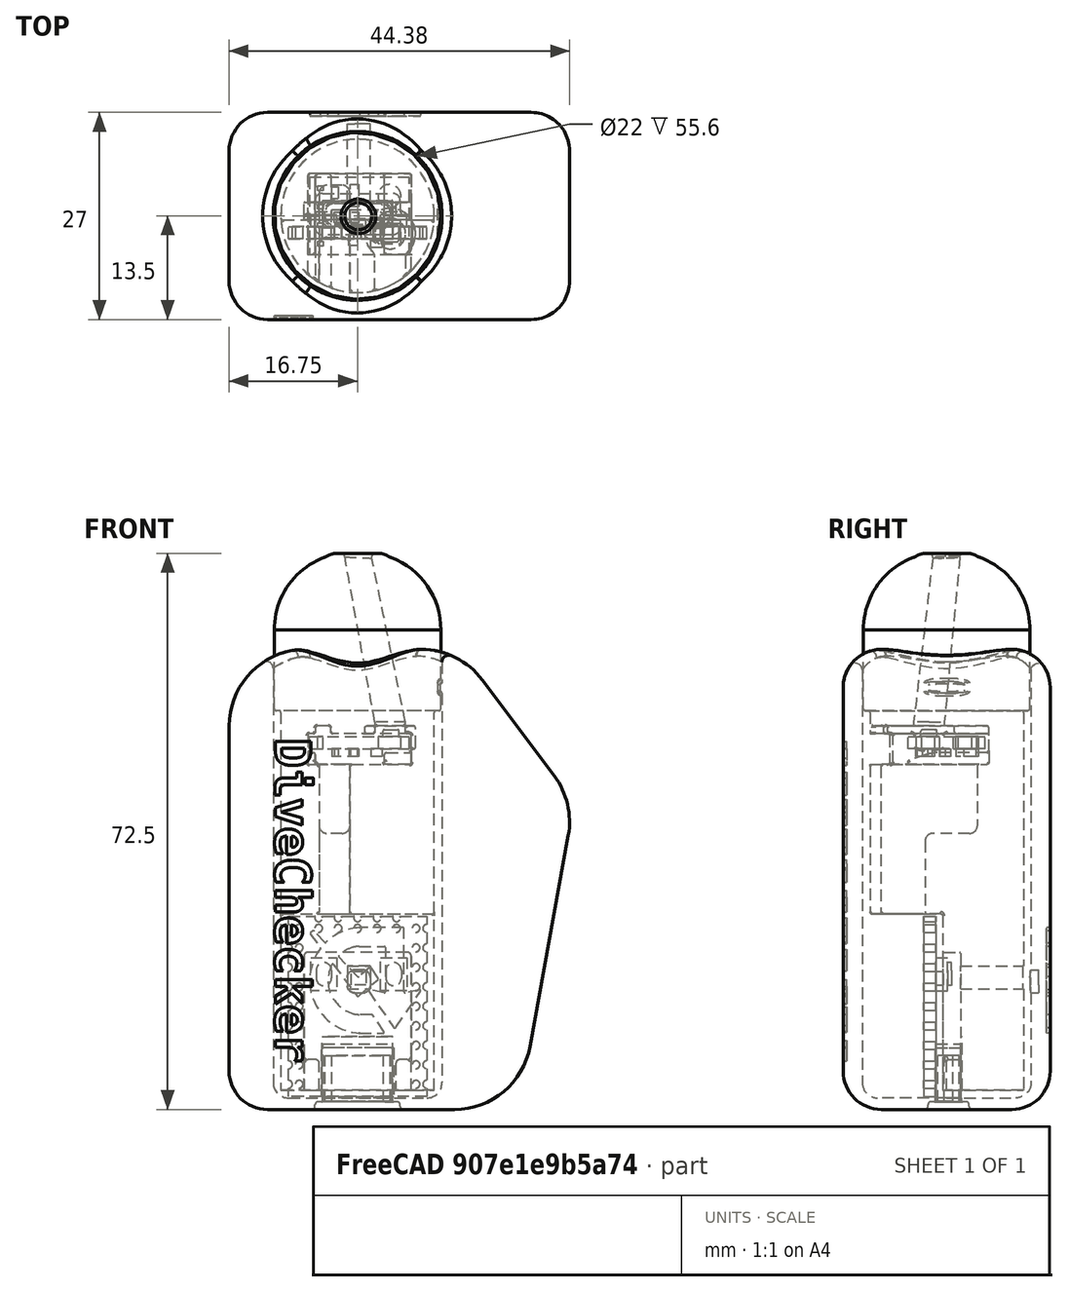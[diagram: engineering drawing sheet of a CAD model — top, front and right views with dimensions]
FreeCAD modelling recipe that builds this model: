
FCSTD DOCUMENT  (FreeCAD 1.0R39319 (Git))
Label: Device_V11
License: All rights reserved
objects: PartDesign::Fillet×55, Sketcher::SketchObject×35, PartDesign::Pocket×26, PartDesign::Pad×14, PartDesign::Revolution×2, Part::Feature×2, PartDesign::SubtractiveLoft×2, PartDesign::Body×2, PartDesign::SubtractivePipe×1, PartDesign::Chamfer×1, Image::ImagePlane×1, Part::Part2DObjectPython×1
note: 378 computed .brp shape members not serialized (recipe doc carries the construction recipe); baked Part::Feature solids carry a one-line shape summary decoded from their .brp

FEATURE [Sketcher::SketchObject] Sketch
  ArcFitTolerance = 1e-06
  AttachmentSupport = -> [XZ_Plane]
  FullyConstrained = true
  MakeInternals = false
  MapMode = 5
  Placement = pos=(0,0,0) rot=(1,0,0;1.5708rad)
  sketch-geometry (8):
    g0: LineSegment [constr] StartX=0 StartY=0 StartZ=0 EndX=0 EndY=75 EndZ=0
    g1: LineSegment StartX=0 StartY=75 StartZ=0 EndX=30 EndY=75 EndZ=0
    g2: LineSegment StartX=30 StartY=75 StartZ=0 EndX=45 EndY=55 EndZ=0
    g3: LineSegment [constr] StartX=45 StartY=55 StartZ=0 EndX=35 EndY=0 EndZ=0
    g4: LineSegment [constr] StartX=35 StartY=0 StartZ=0 EndX=0 EndY=0 EndZ=0
    g5: LineSegment StartX=0 StartY=75 StartZ=0 EndX=0 EndY=15 EndZ=0
    g6: LineSegment StartX=0 StartY=15 StartZ=0 EndX=37.7273 EndY=15 EndZ=0
    g7: LineSegment StartX=37.7273 StartY=15 StartZ=0 EndX=45 EndY=55 EndZ=0
  constraints (22):
    c: Coincident(g-1,g0)
    c: Coincident(g0,g1)
    c: Horizontal(g1)
    c: Coincident(g1,g2)
    c: Coincident(g2,g3)
    c: Coincident(g3,g4)
    c: Coincident(g4,g0)
    c: Vertical(g0)
    c: Horizontal(g4)
    c: DistanceX(g4,g4) = 35
    c: DistanceX(g1,g1) = 30
    c: DistanceY(g0,g0) = 75
    c: DistanceY(g2,g1) = 20
    c: DistanceX(g0,g2) = 45
    c: Coincident(g5,g0)
    c: Coincident(g6,g5)
    c: Horizontal(g6)
    c: Coincident(g7,g6)
    c: Coincident(g7,g2)
    c: PointOnObject(g6,g3)
    c: Vertical(g5)
    c: DistanceY(g0,g5) = 15
FEATURE [PartDesign::Pad] Pad
  Direction = (0,-1,2e-16)
  Length = 27
  Length2 = 10
  Midplane = true
  Placement = pos=(0,0,0) rot=(1,0,0;1.5708rad)
  Profile = -> Sketch
  ReferenceAxis = -> Sketch [N_Axis]
  Refine = true
  Suppressed = false
  Type = 0
FEATURE [PartDesign::Fillet] Fillet
  Base = -> Pad [Edge2,Edge5,Edge8,Edge1]
  BaseFeature = -> Pad
  Placement = pos=(0,0,0) rot=(1,0,0;1.5708rad)
  Radius = 10
  Refine = true
  SupportTransform = false
  Suppressed = false
  UseAllEdges = false
FEATURE [PartDesign::Fillet] Fillet001
  Base = -> Fillet [Edge18,Edge8,Edge23]
  BaseFeature = -> Fillet
  Placement = pos=(0,0,0) rot=(1,0,0;1.5708rad)
  Radius = 5
  Refine = true
  SupportTransform = false
  Suppressed = false
  UseAllEdges = false
FEATURE [Sketcher::SketchObject] Sketch003
  ArcFitTolerance = 1e-06
  AttachmentSupport = -> [XZ_Plane001]
  FullyConstrained = true
  MakeInternals = false
  MapMode = 5
  Placement = pos=(0,0,0) rot=(1,0,0;1.5708rad)
  sketch-geometry (9):
    g0: LineSegment StartX=19 StartY=87 StartZ=0 EndX=19 EndY=77 EndZ=0
    g1: LineSegment StartX=19 StartY=77 StartZ=0 EndX=27.5 EndY=77 EndZ=0
    g2: LineSegment StartX=19 StartY=87 StartZ=0 EndX=20 EndY=87 EndZ=0
    g3: LineSegment StartX=20 StartY=87 StartZ=0 EndX=21 EndY=86.5 EndZ=0
    g4: ArcOfCircle CenterX=17.4538 CenterY=77.1 CenterZ=0 NormalX=0 NormalY=0 NormalZ=1 AngleXU=0 Radius=10.0467 StartAngle=6.27323 EndAngle=7.49324
    g5: LineSegment [constr] StartX=0 StartY=0 StartZ=0 EndX=27.5 EndY=0 EndZ=0
    g6: LineSegment [constr] StartX=27.5 StartY=0 StartZ=0 EndX=27.5 EndY=77 EndZ=0
    g7: LineSegment [constr] StartX=27.5 StartY=77 StartZ=0 EndX=0 EndY=77 EndZ=0
    g8: LineSegment [constr] StartX=0 StartY=77 StartZ=0 EndX=0 EndY=0 EndZ=0
  constraints (26):
    c: Vertical(g0)
    c: Coincident(g0,g1)
    c: Horizontal(g1)
    c: Coincident(g0,g2)
    c: Horizontal(g2)
    c: Coincident(g2,g3)
    c: Coincident(g4,g3)
    c: Coincident(g4,g1)
    c: DistanceY(g0,g0) = 10
    c: DistanceY(g3,g2) = 0.5
    c: DistanceX(g2,g2) = 1
    c: DistanceX(g2,g3) = 1
    c: DistanceX(g1,g1) = 8.5
    c: Coincident(g5,g6)
    c: Coincident(g6,g7)
    c: Coincident(g7,g8)
    c: Coincident(g8,g5)
    c: Horizontal(g5)
    c: Horizontal(g7)
    c: Vertical(g6)
    c: Vertical(g8)
    c: Coincident(g5,g-1)
    c: Coincident(g6,g1)
    c: DistanceY(g8,g8) = 77
    c: DistanceX(g7,g7) = 27.5
    c: DistanceY(g0,g4) = 0.1
FEATURE [Sketcher::SketchObject] Sketch004
  ArcFitTolerance = 1e-06
  AttachmentSupport = -> [XZ_Plane001]
  FullyConstrained = true
  MakeInternals = false
  MapMode = 5
  Placement = pos=(0,0,0) rot=(1,0,0;1.5708rad)
  sketch-geometry (7):
    g0: LineSegment StartX=16.75 StartY=87 StartZ=0 EndX=16.75 EndY=77 EndZ=0
    g1: LineSegment [constr] StartX=0 StartY=0 StartZ=0 EndX=27.5 EndY=0 EndZ=0
    g2: LineSegment [constr] StartX=27.5 StartY=0 StartZ=0 EndX=27.5 EndY=77 EndZ=0
    g3: LineSegment [constr] StartX=27.5 StartY=77 StartZ=0 EndX=0 EndY=77 EndZ=0
    g4: LineSegment [constr] StartX=0 StartY=77 StartZ=0 EndX=0 EndY=0 EndZ=0
    g5: GeomPoint [constr] X=10 Y=77 Z=0
    g6: GeomPoint [constr] X=23.5 Y=77 Z=0
  constraints (18):
    c: Vertical(g0)
    c: DistanceY(g0,g0) = 10
    c: Coincident(g1,g2)
    c: Coincident(g2,g3)
    c: Coincident(g3,g4)
    c: Coincident(g4,g1)
    c: Horizontal(g1)
    c: Horizontal(g3)
    c: Vertical(g2)
    c: Vertical(g4)
    c: Coincident(g1,g-1)
    c: DistanceY(g4,g4) = 77
    c: DistanceX(g3,g3) = 27.5
    c: PointOnObject(g5,g3)
    c: PointOnObject(g6,g3)
    c: DistanceX(g6,g2) = 4
    c: DistanceX(g3,g5) = 10
    c: Symmetric(g5,g6,g0)
FEATURE [PartDesign::Revolution] Revolution
  Angle = 360
  Angle2 = 60
  Axis = (0,-2e-16,-1)
  Base = (16.75,1.93e-14,87)
  Placement = pos=(0,0,0) rot=(1,0,0;1.5708rad)
  Profile = -> Sketch003
  ReferenceAxis = -> Sketch004 [Edge1]
  Refine = true
  Reversed = true
  Suppressed = false
  Type = 0
FEATURE [PartDesign::Pad] Pad001
  BaseFeature = -> Revolution
  Direction = (0,-2e-16,-1)
  Length = 61
  Length2 = 10
  Placement = pos=(0,0,0) rot=(1,0,0;1.5708rad)
  Profile = -> Revolution [Face2]
  Refine = true
  Suppressed = false
  Type = 0
FEATURE [Sketcher::SketchObject] Sketch006
  ArcFitTolerance = 1e-06
  AttachmentOffset = pos=(0,0,-25) rot=(0,0,1;0rad)
  AttachmentSupport = -> [Fillet001]
  FullyConstrained = true
  MakeInternals = false
  MapMode = 5
  Placement = pos=(0,6.6e-15,40) rot=(1,0,0;3.14159rad)
  sketch-geometry (1):
    g0: Circle CenterX=16.75 CenterY=0 CenterZ=0 NormalX=0 NormalY=0 NormalZ=1 AngleXU=0 Radius=11
  constraints (3):
    c: PointOnObject(g0,g-1)
    c: DistanceX(g-1,g0) = 16.75
    c: Diameter(g0) = 22
FEATURE [PartDesign::Pocket] Pocket
  BaseFeature = -> Fillet001
  Direction = (0,0,1)
  Length = 5
  Length2 = 5
  Placement = pos=(0,0,0) rot=(1,0,0;1.5708rad)
  Profile = -> Sketch006
  ReferenceAxis = -> Sketch006 [N_Axis]
  Refine = true
  Suppressed = false
  Type = 1
FEATURE [Part::Feature] Part__Feature  label="RP2350-Zero-mini"
  Placement = pos=(7.75,-3,40.2) rot=(1,0,0;4.71239rad)
  shape: bbox 18 x 4.88 x 24.16 mm, 130 faces (baked)
FEATURE [Sketcher::SketchObject] Sketch008
  ArcFitTolerance = 1e-06
  AttachmentSupport = -> [Pocket]
  ExternalGeometry = -> [Pocket]
  FullyConstrained = true
  MakeInternals = false
  MapMode = 5
  Placement = pos=(0,0,40) rot=(0,0,1;3.14159rad)
  sketch-geometry (19):
    g0: LineSegment [constr] StartX=-25.85 StartY=5.5 StartZ=0 EndX=-7.65 EndY=5.5 EndZ=0
    g1: LineSegment StartX=-7.65 StartY=5.5 StartZ=0 EndX=-7.65 EndY=1.3 EndZ=0
    g2: LineSegment [constr] StartX=-7.65 StartY=1.3 StartZ=0 EndX=-9.75 EndY=1.3 EndZ=0
    g3: LineSegment [constr] StartX=-9.75 StartY=1.3 StartZ=0 EndX=-9.75 EndY=-1.5 EndZ=0
    g4: LineSegment [constr] StartX=-9.75 StartY=-1.5 StartZ=0 EndX=-11.75 EndY=-1.5 EndZ=0
    g5: LineSegment [constr] StartX=-11.75 StartY=-1.5 StartZ=0 EndX=-11.75 EndY=-2.5 EndZ=0
    g6: LineSegment StartX=-11.75 StartY=-2.5 StartZ=0 EndX=-21.75 EndY=-2.5 EndZ=0
    g7: LineSegment [constr] StartX=-21.75 StartY=-2.5 StartZ=0 EndX=-21.75 EndY=-1.5 EndZ=0
    g8: LineSegment [constr] StartX=-21.75 StartY=-1.5 StartZ=0 EndX=-23.75 EndY=-1.5 EndZ=0
    g9: LineSegment [constr] StartX=-23.75 StartY=-1.5 StartZ=0 EndX=-23.75 EndY=1.3 EndZ=0
    g10: LineSegment [constr] StartX=-23.75 StartY=1.3 StartZ=0 EndX=-25.85 EndY=1.3 EndZ=0
    g11: LineSegment StartX=-25.85 StartY=1.3 StartZ=0 EndX=-25.85 EndY=5.5 EndZ=0
    g12: LineSegment StartX=-25.85 StartY=5.5 StartZ=0 EndX=-20.85 EndY=3.5 EndZ=0
    g13: LineSegment StartX=-20.85 StartY=3.5 StartZ=0 EndX=-12.65 EndY=3.5 EndZ=0
    g14: LineSegment StartX=-12.65 StartY=3.5 StartZ=0 EndX=-7.65 EndY=5.5 EndZ=0
    g15: LineSegment StartX=-25.85 StartY=1.3 StartZ=0 EndX=-21.75 EndY=1.3 EndZ=0
    g16: LineSegment StartX=-21.75 StartY=1.3 StartZ=0 EndX=-21.75 EndY=-2.5 EndZ=0
    g17: LineSegment StartX=-11.75 StartY=-2.5 StartZ=0 EndX=-11.75 EndY=1.3 EndZ=0
    g18: LineSegment StartX=-11.75 StartY=1.3 StartZ=0 EndX=-7.65 EndY=1.3 EndZ=0
  constraints (54):
    c: Horizontal(g0)
    c: Coincident(g0,g1)
    c: Vertical(g1)
    c: Coincident(g1,g2)
    c: Horizontal(g2)
    c: Coincident(g2,g3)
    c: Vertical(g3)
    c: Coincident(g3,g4)
    c: Horizontal(g4)
    c: Coincident(g4,g5)
    c: Vertical(g5)
    c: Coincident(g5,g6)
    c: Horizontal(g6)
    c: Coincident(g6,g7)
    c: Vertical(g7)
    c: Coincident(g7,g8)
    c: Horizontal(g8)
    c: Coincident(g8,g9)
    c: Vertical(g9)
    c: Coincident(g9,g10)
    c: Horizontal(g10)
    c: Coincident(g10,g11)
    c: Vertical(g11)
    c: Coincident(g0,g11)
    c: DistanceX(g0,g-3) = 9.1
    c: DistanceX(g0,g0) = 18.2
    c: DistanceY(g-3,g1) = 1.3
    c: Horizontal(g2,g9)
    c: DistanceX(g8,g-3) = 7
    c: DistanceX(g-3,g3) = 7
    c: DistanceY(g3,g-3) = 1.5
    c: Horizontal(g3,g7)
    c: DistanceX(g7,g-3) = 5
    c: DistanceX(g-3,g4) = 5
    c: DistanceY(g5,g-3) = 2.5
    c: DistanceY(g-3,g0) = 5.5
    c: Coincident(g0,g12)
    c: Coincident(g12,g13)
    c: Horizontal(g13)
    c: Coincident(g13,g14)
    c: Coincident(g14,g0)
    c: DistanceX(g13,g0) = 5
    c: DistanceX(g0,g12) = 5
    c: DistanceY(g12,g0) = 2
    c: Coincident(g15,g10)
    c: Horizontal(g15)
    c: Coincident(g16,g15)
    c: Coincident(g16,g6)
    c: Vertical(g16)
    c: Coincident(g17,g5)
    c: Vertical(g17)
    c: Coincident(g18,g17)
    c: Coincident(g18,g1)
    c: Horizontal(g18)
FEATURE [PartDesign::Pocket] Pocket001
  BaseFeature = -> Pocket
  Direction = (0,0,-1)
  Length = 24
  Length2 = 5
  Placement = pos=(0,0,0) rot=(1,0,0;1.5708rad)
  Profile = -> Sketch008
  ReferenceAxis = -> Sketch008 [N_Axis]
  Refine = true
  Suppressed = false
  Type = 0
FEATURE [Sketcher::SketchObject] Sketch009
  ArcFitTolerance = 1e-06
  AttachmentSupport = -> [Pocket001]
  ExternalGeometry = -> [Pocket001]
  FullyConstrained = true
  MakeInternals = false
  MapMode = 5
  Placement = pos=(0,0,40) rot=(0,0,1;3.14159rad)
  sketch-geometry (8):
    g0: LineSegment StartX=-21.75 StartY=1.3 StartZ=0 EndX=-23.45 EndY=1.3 EndZ=0
    g1: LineSegment StartX=-23.45 StartY=1.3 StartZ=0 EndX=-23.45 EndY=-1.7 EndZ=0
    g2: LineSegment StartX=-23.45 StartY=-1.7 StartZ=0 EndX=-21.75 EndY=-1.7 EndZ=0
    g3: LineSegment StartX=-21.75 StartY=-1.7 StartZ=0 EndX=-21.75 EndY=1.3 EndZ=0
    g4: LineSegment StartX=-11.75 StartY=1.3 StartZ=0 EndX=-11.75 EndY=-1.7 EndZ=0
    g5: LineSegment StartX=-11.75 StartY=-1.7 StartZ=0 EndX=-10.05 EndY=-1.7 EndZ=0
    g6: LineSegment StartX=-10.05 StartY=-1.7 StartZ=0 EndX=-10.05 EndY=1.3 EndZ=0
    g7: LineSegment StartX=-10.05 StartY=1.3 StartZ=0 EndX=-11.75 EndY=1.3 EndZ=0
  constraints (22):
    c: Coincident(g0,g1)
    c: Coincident(g1,g2)
    c: Coincident(g2,g3)
    c: Coincident(g3,g0)
    c: Horizontal(g0)
    c: Horizontal(g2)
    c: Vertical(g1)
    c: Vertical(g3)
    c: Coincident(g0,g-3)
    c: DistanceY(g1,g1) = 3
    c: DistanceX(g2,g2) = 1.7
    c: Coincident(g4,g5)
    c: Coincident(g5,g6)
    c: Coincident(g6,g7)
    c: Coincident(g7,g4)
    c: Vertical(g4)
    c: Vertical(g6)
    c: Horizontal(g5)
    c: Horizontal(g7)
    c: Coincident(g4,g-4)
    c: Equal(g2,g5)
    c: Equal(g1,g6)
FEATURE [PartDesign::Pocket] Pocket002
  BaseFeature = -> Pocket001
  Direction = (0,0,-1)
  Length = 16
  Length2 = 5
  Placement = pos=(0,0,0) rot=(1,0,0;1.5708rad)
  Profile = -> Sketch009
  ReferenceAxis = -> Sketch009 [N_Axis]
  Refine = true
  Suppressed = false
  Type = 0
FEATURE [Sketcher::SketchObject] Sketch010
  ArcFitTolerance = 1e-06
  AttachmentSupport = -> [Pocket002]
  ExternalGeometry = -> [Pocket002]
  FullyConstrained = true
  MakeInternals = false
  MapMode = 5
  Placement = pos=(0,6.6e-15,15) rot=(1,0,0;3.14159rad)
  sketch-geometry (4):
    g0: LineSegment StartX=12.2 StartY=1.45 StartZ=0 EndX=12.2 EndY=-1.94 EndZ=0
    g1: LineSegment StartX=12.2 StartY=-1.94 StartZ=0 EndX=21.3 EndY=-1.94 EndZ=0
    g2: LineSegment StartX=21.3 StartY=-1.94 StartZ=0 EndX=21.3 EndY=1.45 EndZ=0
    g3: LineSegment StartX=21.3 StartY=1.45 StartZ=0 EndX=12.2 EndY=1.45 EndZ=0
  constraints (12):
    c: Coincident(g0,g1)
    c: Coincident(g1,g2)
    c: Coincident(g2,g3)
    c: Coincident(g3,g0)
    c: Vertical(g0)
    c: Vertical(g2)
    c: Horizontal(g1)
    c: Horizontal(g3)
    c: DistanceY(g2,g2) = 3.39
    c: DistanceX(g3,g3) = 9.1
    c: DistanceX(g-5,g0) = 0.45
    c: DistanceY(g-4,g1) = 0.56
FEATURE [PartDesign::Pocket] Pocket003
  BaseFeature = -> Pocket002
  Direction = (0,0,1)
  Length = 1
  Length2 = 5
  Placement = pos=(0,0,0) rot=(1,0,0;1.5708rad)
  Profile = -> Sketch010
  ReferenceAxis = -> Sketch010 [N_Axis]
  Refine = true
  Suppressed = false
  Type = 0
FEATURE [PartDesign::Fillet] Fillet002
  Base = -> Pocket003 [Edge141,Edge140]
  BaseFeature = -> Pocket003
  Placement = pos=(0,0,0) rot=(1,0,0;1.5708rad)
  Radius = 1
  Refine = true
  SupportTransform = false
  Suppressed = false
  UseAllEdges = false
FEATURE [PartDesign::Fillet] Fillet003
  Base = -> Fillet002 [Edge16,Edge12]
  BaseFeature = -> Fillet002
  Placement = pos=(0,0,0) rot=(1,0,0;1.5708rad)
  Radius = 1
  Refine = true
  SupportTransform = false
  Suppressed = false
  UseAllEdges = false
FEATURE [PartDesign::Fillet] Fillet004
  Base = -> Fillet003 [Edge85,Edge101]
  BaseFeature = -> Fillet003
  Placement = pos=(0,0,0) rot=(1,0,0;1.5708rad)
  Radius = 1
  Refine = true
  SupportTransform = false
  Suppressed = false
  UseAllEdges = false
FEATURE [PartDesign::Fillet] Fillet005
  Base = -> Fillet004 [Edge33,Edge36]
  BaseFeature = -> Fillet004
  Placement = pos=(0,0,0) rot=(1,0,0;1.5708rad)
  Radius = 0.5
  Refine = true
  SupportTransform = false
  Suppressed = false
  UseAllEdges = false
FEATURE [PartDesign::Fillet] Fillet006
  Base = -> Fillet005 [Edge85,Edge82]
  BaseFeature = -> Fillet005
  Placement = pos=(0,0,0) rot=(1,0,0;1.5708rad)
  Radius = 0.5
  Refine = true
  SupportTransform = false
  Suppressed = false
  UseAllEdges = false
FEATURE [PartDesign::Fillet] Fillet007
  Base = -> Fillet006 [Edge24,Edge56]
  BaseFeature = -> Fillet006
  Placement = pos=(0,0,0) rot=(1,0,0;1.5708rad)
  Radius = 0.25
  Refine = true
  SupportTransform = false
  Suppressed = false
  UseAllEdges = false
FEATURE [PartDesign::Fillet] Fillet008
  Base = -> Fillet007 [Edge38,Edge95]
  BaseFeature = -> Fillet007
  Placement = pos=(0,0,0) rot=(1,0,0;1.5708rad)
  Radius = 0.5
  Refine = true
  SupportTransform = false
  Suppressed = false
  UseAllEdges = false
FEATURE [PartDesign::Fillet] Fillet009
  Base = -> Fillet008 [Edge79,Edge60]
  BaseFeature = -> Fillet008
  Placement = pos=(0,0,0) rot=(1,0,0;1.5708rad)
  Radius = 0.13
  Refine = true
  SupportTransform = false
  Suppressed = false
  UseAllEdges = false
FEATURE [Part::Feature] Part__Feature001  label="BME280-5V"
  Placement = pos=(10.5,-5,62) rot=(0,0,1;0rad)
  shape: bbox 13 x 10 x 3.53 mm, 88 faces (baked)
FEATURE [Sketcher::SketchObject] Sketch012
  ArcFitTolerance = 1e-06
  AttachmentSupport = -> [XZ_Plane001]
  FullyConstrained = true
  MakeInternals = false
  MapMode = 5
  Placement = pos=(0,0,0) rot=(1,0,0;1.5708rad)
  sketch-geometry (4):
    g0: LineSegment StartX=10.25 StartY=63.5 StartZ=0 EndX=10.25 EndY=59.5 EndZ=0
    g1: LineSegment StartX=10.25 StartY=59.5 StartZ=0 EndX=23.75 EndY=59.5 EndZ=0
    g2: LineSegment StartX=23.75 StartY=59.5 StartZ=0 EndX=23.75 EndY=63.5 EndZ=0
    g3: LineSegment StartX=23.75 StartY=63.5 StartZ=0 EndX=10.25 EndY=63.5 EndZ=0
  constraints (12):
    c: Coincident(g0,g1)
    c: Coincident(g1,g2)
    c: Coincident(g2,g3)
    c: Coincident(g3,g0)
    c: Vertical(g0)
    c: Vertical(g2)
    c: Horizontal(g1)
    c: Horizontal(g3)
    c: Distance(g0,g2) = 13.5
    c: Distance(g1,g3) = 4
    c: DistanceY(g-1,g0) = 59.5
    c: DistanceX(g-1,g0) = 10.25
FEATURE [PartDesign::Pocket] Pocket004
  BaseFeature = -> Pad001
  Direction = (0,1,-2e-16)
  Length = 5
  Length2 = 13
  Placement = pos=(0,0,0) rot=(1,0,0;1.5708rad)
  Profile = -> Sketch012
  ReferenceAxis = -> Sketch012 [N_Axis]
  Refine = true
  Suppressed = false
  Type = 4
FEATURE [Sketcher::SketchObject] Sketch013
  ArcFitTolerance = 1e-06
  AttachmentSupport = -> [Pocket004]
  FullyConstrained = true
  MakeInternals = false
  MapMode = 5
  Placement = pos=(0,2.79e-14,63.5) rot=(1,0,0;3.14159rad)
  sketch-geometry (2):
    g0: Circle CenterX=21 CenterY=2.3 CenterZ=0 NormalX=0 NormalY=0 NormalZ=1 AngleXU=0 Radius=2
    g1: Circle CenterX=21 CenterY=2.3 CenterZ=0 NormalX=0 NormalY=0 NormalZ=1 AngleXU=0 Radius=3.3
  constraints (5):
    c: Diameter(g0) = 4
    c: DistanceY(g-1,g0) = 2.3
    c: DistanceX(g-1,g0) = 21
    c: Diameter(g1) = 6.6
    c: Coincident(g1,g0)
FEATURE [Sketcher::SketchObject] Sketch015
  ArcFitTolerance = 1e-06
  AttachmentSupport = -> [Pocket004]
  ExternalGeometry = -> [Pocket004]
  FullyConstrained = true
  MakeInternals = false
  MapMode = 5
  Placement = pos=(0,3.83e-14,87) rot=(0,0,1;3.14159rad)
  sketch-geometry (1):
    g0: Circle CenterX=-16.75 CenterY=0 CenterZ=0 NormalX=0 NormalY=0 NormalZ=1 AngleXU=0 Radius=2.25
  constraints (2):
    c: Coincident(g0,g-3)
    c: Equal(g0,g-3)
FEATURE [PartDesign::Pad] Pad002
  BaseFeature = -> Pocket004
  Direction = (0,0,1)
  Length = 23.5
  Length2 = 10
  Placement = pos=(0,0,0) rot=(1,0,0;1.5708rad)
  Profile = -> Sketch015
  ReferenceAxis = -> Sketch015 [N_Axis]
  Refine = true
  Reversed = true
  Suppressed = false
  Type = 0
FEATURE [PartDesign::Pocket] Pocket005
  BaseFeature = -> Pad002
  Direction = (0,0,1)
  Length = 1
  Length2 = 5
  Placement = pos=(0,0,0) rot=(1,0,0;1.5708rad)
  Profile = -> Sketch013
  ReferenceAxis = -> Sketch013 [N_Axis]
  Refine = true
  Suppressed = false
  Type = 0
FEATURE [Sketcher::SketchObject] Sketch016
  ArcFitTolerance = 1e-06
  AttachmentSupport = -> [Pocket005]
  ExternalGeometry = -> [Pocket005]
  FullyConstrained = true
  MakeInternals = false
  MapMode = 5
  Placement = pos=(0,3.18e-14,63.5) rot=(1,0,0;3.14159rad)
  sketch-geometry (1):
    g0: Circle CenterX=21 CenterY=2.3 CenterZ=0 NormalX=0 NormalY=0 NormalZ=1 AngleXU=0 Radius=2
  constraints (2):
    c: Coincident(g0,g-3)
    c: Equal(g0,g-3)
FEATURE [PartDesign::Pocket] Pocket006
  BaseFeature = -> Pocket005
  Direction = (0,0,1)
  Length = 5
  Length2 = 5
  Placement = pos=(0,0,0) rot=(1,0,0;1.5708rad)
  Profile = -> Sketch016
  ReferenceAxis = -> Sketch016 [N_Axis]
  Refine = true
  Suppressed = false
  Type = 0
FEATURE [Sketcher::SketchObject] Sketch017
  ArcFitTolerance = 1e-06
  AttachmentSupport = -> [XZ_Plane001]
  ExternalGeometry = -> [Pocket006]
  FullyConstrained = true
  MakeInternals = false
  MapMode = 5
  Placement = pos=(0,0,0) rot=(1,0,0;1.5708rad)
  sketch-geometry (7):
    g0: LineSegment StartX=9.25 StartY=75.5 StartZ=0 EndX=9.46286 EndY=70.5 EndZ=0
    g1: LineSegment StartX=15.2301 StartY=70.6227 StartZ=0 EndX=15.2301 EndY=75 EndZ=0
    g2: LineSegment StartX=21 StartY=75 StartZ=0 EndX=21 EndY=68.5 EndZ=0
    g3: ArcOfCircle CenterX=12.3452 CenterY=70.6227 CenterZ=0 NormalX=0 NormalY=0 NormalZ=1 AngleXU=0 Radius=2.88494 StartAngle=3.18414 EndAngle=6.28319
    g4: ArcOfCircle CenterX=18.1151 CenterY=75 CenterZ=0 NormalX=0 NormalY=0 NormalZ=1 AngleXU=0 Radius=2.88494 StartAngle=1.6e-15 EndAngle=3.14159
    g5: ArcOfCircle CenterX=14.9407 CenterY=75.7423 CenterZ=0 NormalX=0 NormalY=0 NormalZ=1 AngleXU=0 Radius=5.69588 StartAngle=1.96559 EndAngle=3.18414
    g6: ArcOfCircle CenterX=10.25 CenterY=87 CenterZ=0 NormalX=0 NormalY=0 NormalZ=1 AngleXU=0 Radius=6.5 StartAngle=5.10718 EndAngle=6.28319
  constraints (18):
    c: Vertical(g1)
    c: Vertical(g2)
    c: Symmetric(g-3,g-3,g2)
    c: Tangent(g3,g0) = -1.5708
    c: Tangent(g3,g1) = -1.5708
    c: Tangent(g4,g1) = 1.5708
    c: Tangent(g4,g2) = 1.5708
    c: Symmetric(g-4,g-4,g6)
    c: Tangent(g6,g5) = 1.5708
    c: DistanceY(g-1,g2) = 75
    c: Perpendicular(g6,g-4)
    c: Tangent(g5,g0) = -1.5708
    c: DistanceY(g5,g6) = 6
    c: DistanceX(g5,g6) = 4
    c: DistanceY(g0,g5) = 5.5
    c: DistanceX(g0,g5) = 3.5
    c: DistanceY(g0,g0) = 5
    c: Equal(g3,g4)
FEATURE [Sketcher::SketchObject] Sketch018
  ArcFitTolerance = 1e-06
  AttachmentSupport = -> [Pocket006]
  ExternalGeometry = -> [Pocket006]
  FullyConstrained = true
  MakeInternals = false
  MapMode = 5
  Placement = pos=(0,3.83e-14,87) rot=(0,0,1;3.14159rad)
  sketch-geometry (1):
    g0: Circle CenterX=-16.75 CenterY=0 CenterZ=0 NormalX=0 NormalY=0 NormalZ=1 AngleXU=0 Radius=1.75
  constraints (2):
    c: Coincident(g0,g-3)
    c: Diameter(g0) = 3.5
FEATURE [PartDesign::SubtractivePipe] SubtractivePipe
  AuxilleryCurvelinear = true
  AuxillerySpineTangent = false
  BaseFeature = -> Pocket006
  Binormal = (0,0,0)
  Mode = 0
  Placement = pos=(0,0,0) rot=(1,0,0;1.5708rad)
  Profile = -> Sketch018
  Refine = true
  Spine = -> Sketch017 [Edge1,Edge2,Edge3,Edge4,Edge5,Edge6]
  SpineTangent = false
  Suppressed = false
  Transformation = 1
  Transition = 0
FEATURE [PartDesign::SubtractiveLoft] SubtractiveLoft
  BaseFeature = -> SubtractivePipe
  Closed = false
  Placement = pos=(0,0,0) rot=(1,0,0;1.5708rad)
  Profile = -> SubtractivePipe [Edge45]
  Refine = true
  Ruled = false
  Sections = -> [SubtractivePipe]
  Suppressed = false
FEATURE [Sketcher::SketchObject] Sketch019
  ArcFitTolerance = 1e-06
  AttachmentSupport = -> [SubtractiveLoft]
  ExternalGeometry = -> [SubtractiveLoft]
  FullyConstrained = true
  MakeInternals = false
  MapMode = 5
  Placement = pos=(0,2.62e-14,59.5) rot=(0,0,1;3.14159rad)
  sketch-geometry (8):
    g0: LineSegment StartX=-23.75 StartY=-5 StartZ=0 EndX=-20.25 EndY=-5 EndZ=0
    g1: LineSegment StartX=-20.25 StartY=-5 StartZ=0 EndX=-20.25 EndY=5 EndZ=0
    g2: LineSegment StartX=-20.25 StartY=5 StartZ=0 EndX=-23.75 EndY=5 EndZ=0
    g3: LineSegment StartX=-23.75 StartY=5 StartZ=0 EndX=-23.75 EndY=-5 EndZ=0
    g4: LineSegment StartX=-10.25 StartY=-5 StartZ=0 EndX=-10.25 EndY=5 EndZ=0
    g5: LineSegment StartX=-10.25 StartY=5 StartZ=0 EndX=-10.75 EndY=5 EndZ=0
    g6: LineSegment StartX=-10.75 StartY=5 StartZ=0 EndX=-10.75 EndY=-5 EndZ=0
    g7: LineSegment StartX=-10.75 StartY=-5 StartZ=0 EndX=-10.25 EndY=-5 EndZ=0
  constraints (22):
    c: Coincident(g0,g1)
    c: Coincident(g1,g2)
    c: Coincident(g2,g3)
    c: Coincident(g3,g0)
    c: Horizontal(g0)
    c: Horizontal(g2)
    c: Vertical(g1)
    c: Vertical(g3)
    c: Coincident(g0,g-3)
    c: Coincident(g4,g5)
    c: Coincident(g5,g6)
    c: Coincident(g6,g7)
    c: Coincident(g7,g4)
    c: Vertical(g4)
    c: Vertical(g6)
    c: Horizontal(g5)
    c: Horizontal(g7)
    c: Distance(g4,g6) = 0.5
    c: Coincident(g4,g-3)
    c: Equal(g6,g1)
    c: DistanceY(g4,g4) = 10
    c: DistanceX(g2,g2) = 3.5
FEATURE [PartDesign::Pad] Pad003
  BaseFeature = -> SubtractiveLoft
  Direction = (0,0,1)
  Length = 1.5
  Length2 = 10
  Placement = pos=(0,0,0) rot=(1,0,0;1.5708rad)
  Profile = -> Sketch019
  ReferenceAxis = -> Sketch019 [N_Axis]
  Refine = true
  Suppressed = false
  Type = 0
FEATURE [Sketcher::SketchObject] Sketch024
  ArcFitTolerance = 1e-06
  AttachmentSupport = -> [XZ_Plane001]
  FullyConstrained = true
  MakeInternals = false
  MapMode = 5
  Placement = pos=(0,0,0) rot=(1,0,0;1.5708rad)
  sketch-geometry (6):
    g0: LineSegment StartX=16.75 StartY=87 StartZ=0 EndX=16.75 EndY=65 EndZ=0
    g1: LineSegment StartX=16.75 StartY=65 StartZ=0 EndX=27.6 EndY=65 EndZ=0
    g2: LineSegment StartX=27.6 StartY=65 StartZ=0 EndX=27.6 EndY=77 EndZ=0
    g3: ArcOfCircle CenterX=17.6068 CenterY=77.1 CenterZ=0 NormalX=0 NormalY=0 NormalZ=1 AngleXU=0 Radius=9.99368 StartAngle=6.27318 EndAngle=7.50756
    g4: LineSegment StartX=20 StartY=87 StartZ=0 EndX=21 EndY=86.5 EndZ=0
    g5: LineSegment StartX=20 StartY=87 StartZ=0 EndX=16.75 EndY=87 EndZ=0
  constraints (15):
    c: Vertical(g0)
    c: Symmetric(g-3,g-3,g0)
    c: Horizontal(g-4,g0)
    c: Coincident(g1,g0)
    c: PointOnObject(g1,g-6)
    c: Horizontal(g1)
    c: Coincident(g2,g1)
    c: Coincident(g-6,g2)
    c: Coincident(g3,g-5)
    c: Coincident(g3,g2)
    c: Equal(g-5,g3)
    c: Coincident(g4,g-3)
    c: Coincident(g4,g3)
    c: Coincident(g5,g4)
    c: Coincident(g5,g0)
FEATURE [PartDesign::Revolution] Revolution001
  Angle = 360
  Angle2 = 60
  Axis = (0,-2e-16,-1)
  Base = (16.75,1.93e-14,87)
  BaseFeature = -> Pad003
  Placement = pos=(0,0,0) rot=(1,0,0;1.5708rad)
  Profile = -> Sketch024
  ReferenceAxis = -> Sketch024 [Edge1]
  Refine = true
  Reversed = true
  Suppressed = false
  Type = 0
FEATURE [Sketcher::SketchObject] Sketch026
  ArcFitTolerance = 1e-06
  AttachmentSupport = -> [Revolution001]
  ExternalGeometry = -> [Revolution001]
  FullyConstrained = true
  MakeInternals = false
  MapMode = 5
  Placement = pos=(0,3.83e-14,87) rot=(0,0,1;3.14159rad)
  sketch-geometry (1):
    g0: Circle CenterX=-16.75 CenterY=0 CenterZ=0 NormalX=0 NormalY=0 NormalZ=1 AngleXU=0 Radius=1.75
  constraints (2):
    c: Coincident(g0,g-3)
    c: Diameter(g0) = 3.5
FEATURE [PartDesign::SubtractiveLoft] SubtractiveLoft001
  BaseFeature = -> Revolution001
  Closed = false
  Placement = pos=(0,0,0) rot=(1,0,0;1.5708rad)
  Profile = -> Revolution001 [Edge53]
  Refine = true
  Ruled = false
  Sections = -> [Sketch026]
  Suppressed = false
FEATURE [Sketcher::SketchObject] Sketch028
  ArcFitTolerance = 1e-06
  AttachmentOffset = pos=(0,0,-4) rot=(0,0,1;0rad)
  AttachmentSupport = -> [XZ_Plane001]
  FullyConstrained = true
  MakeInternals = false
  MapMode = 5
  Placement = pos=(0,4,-9e-16) rot=(1,0,0;1.5708rad)
  sketch-geometry (4):
    g0: LineSegment StartX=11.75 StartY=59.5 StartZ=0 EndX=11.75 EndY=55.5 EndZ=0
    g1: LineSegment StartX=11.75 StartY=55.5 StartZ=0 EndX=15.75 EndY=55.5 EndZ=0
    g2: LineSegment StartX=15.75 StartY=55.5 StartZ=0 EndX=15.75 EndY=59.5 EndZ=0
    g3: LineSegment StartX=15.75 StartY=59.5 StartZ=0 EndX=11.75 EndY=59.5 EndZ=0
  constraints (12):
    c: Coincident(g0,g1)
    c: Coincident(g1,g2)
    c: Coincident(g2,g3)
    c: Coincident(g3,g0)
    c: Vertical(g0)
    c: Vertical(g2)
    c: Horizontal(g1)
    c: Horizontal(g3)
    c: PointOnObject(g0,g-3)
    c: DistanceY(g0,g0) = 4
    c: DistanceX(g1,g1) = 4
    c: Vertical(g-4,g0)
FEATURE [Sketcher::SketchObject] Sketch027
  ArcFitTolerance = 1e-06
  FullyConstrained = true
  MakeInternals = false
  MapMode = 5
  Placement = pos=(0,1.78e-14,40.5) rot=(1,0,0;3.14159rad)
  sketch-geometry (1):
    g0: Circle CenterX=16.75 CenterY=0 CenterZ=0 NormalX=0 NormalY=0 NormalZ=1 AngleXU=0 Radius=2.25
  constraints (3):
    c: PointOnObject(g0,g-1)
    c: Vertical(g0,g-3)
    c: Equal(g0,g-4)
FEATURE [PartDesign::Pad] Pad004
  BaseFeature = -> SubtractiveLoft001
  Direction = (0,-1e-16,-1)
  Length = 19
  Length2 = 10
  Placement = pos=(0,0,0) rot=(1,0,0;1.5708rad)
  Profile = -> Sketch027
  ReferenceAxis = -> Sketch027 [N_Axis]
  Refine = true
  Reversed = true
  Suppressed = false
  Type = 0
FEATURE [PartDesign::Pocket] Pocket008
  BaseFeature = -> Pad004
  Direction = (0,1,-2e-16)
  Length = 15
  Length2 = 5
  Placement = pos=(0,0,0) rot=(1,0,0;1.5708rad)
  Profile = -> Sketch028
  ReferenceAxis = -> Sketch028 [N_Axis]
  Refine = true
  Reversed = true
  Suppressed = false
  Type = 0
FEATURE [PartDesign::Pocket] Pocket009
  BaseFeature = -> Pocket008
  Direction = (0,0,1)
  Length = 3
  Length2 = 5
  Placement = pos=(0,0,0) rot=(1,0,0;1.5708rad)
  Profile = -> Pocket008 [Face27]
  Refine = true
  Reversed = true
  Suppressed = false
  Type = 0
FEATURE [Sketcher::SketchObject] Sketch029
  ArcFitTolerance = 1e-06
  FullyConstrained = true
  MakeInternals = false
  MapMode = 5
  Placement = pos=(0,1.23e-14,55.5) rot=(0,0,1;3.14159rad)
  sketch-geometry (4):
    g0: LineSegment StartX=-15.75 StartY=10.8038 StartZ=0 EndX=-15.75 EndY=2.80382 EndZ=0
    g1: LineSegment StartX=-15.75 StartY=2.80382 StartZ=0 EndX=-11.75 EndY=2.80382 EndZ=0
    g2: LineSegment StartX=-11.75 StartY=2.80382 StartZ=0 EndX=-11.75 EndY=10.8038 EndZ=0
    g3: LineSegment StartX=-11.75 StartY=10.8038 StartZ=0 EndX=-15.75 EndY=10.8038 EndZ=0
  constraints (11):
    c: Coincident(g0,g1)
    c: Coincident(g1,g2)
    c: Coincident(g2,g3)
    c: Coincident(g3,g0)
    c: Vertical(g0)
    c: Vertical(g2)
    c: Horizontal(g1)
    c: Horizontal(g3)
    c: Coincident(g0,g-3)
    c: Vertical(g2,g-3)
    c: DistanceY(g2,g2) = 8
FEATURE [PartDesign::Pocket] Pocket010
  BaseFeature = -> Pocket009
  Direction = (0,0,-1)
  Length = 17
  Length2 = 5
  Placement = pos=(0,0,0) rot=(1,0,0;1.5708rad)
  Profile = -> Sketch029
  ReferenceAxis = -> Sketch029 [N_Axis]
  Refine = true
  Suppressed = false
  Type = 0
FEATURE [PartDesign::Fillet] Fillet010
  Base = -> Fillet009 [Edge42,Edge38]
  BaseFeature = -> Fillet009
  Placement = pos=(0,0,0) rot=(1,0,0;1.5708rad)
  Radius = 10
  Refine = true
  SupportTransform = false
  Suppressed = false
  UseAllEdges = false
FEATURE [PartDesign::Fillet] Fillet011
  Base = -> Fillet010 [Edge27,Edge44]
  BaseFeature = -> Fillet010
  Placement = pos=(0,0,0) rot=(1,0,0;1.5708rad)
  Radius = 1
  Refine = true
  SupportTransform = false
  Suppressed = false
  UseAllEdges = false
FEATURE [PartDesign::Fillet] Fillet012
  Base = -> Fillet011 [Edge80]
  BaseFeature = -> Fillet011
  Placement = pos=(0,0,0) rot=(1,0,0;1.5708rad)
  Radius = 0.25
  Refine = true
  SupportTransform = false
  Suppressed = false
  UseAllEdges = false
FEATURE [PartDesign::Fillet] Fillet013
  Base = -> Fillet012 [Edge30]
  BaseFeature = -> Fillet012
  Placement = pos=(0,0,0) rot=(1,0,0;1.5708rad)
  Radius = 0.5
  Refine = true
  SupportTransform = false
  Suppressed = false
  UseAllEdges = false
FEATURE [PartDesign::Fillet] Fillet014
  Base = -> Fillet013 [Edge44]
  BaseFeature = -> Fillet013
  Placement = pos=(0,0,0) rot=(1,0,0;1.5708rad)
  Radius = 0.5
  Refine = true
  SupportTransform = false
  Suppressed = false
  UseAllEdges = false
FEATURE [PartDesign::Fillet] Fillet015
  Base = -> Fillet014 [Edge88]
  BaseFeature = -> Fillet014
  Placement = pos=(0,0,0) rot=(1,0,0;1.5708rad)
  Radius = 0.9
  Refine = true
  SupportTransform = false
  Suppressed = false
  UseAllEdges = false
FEATURE [Sketcher::SketchObject] Sketch021
  ArcFitTolerance = 1e-06
  AttachmentSupport = -> [Fillet015]
  ExternalGeometry = -> [Fillet015]
  FullyConstrained = true
  MakeInternals = false
  MapMode = 5
  Placement = pos=(0,6.6e-15,15) rot=(1,0,0;3.14159rad)
  sketch-geometry (10):
    g0: LineSegment StartX=12.2 StartY=-2.94 StartZ=0 EndX=21.3 EndY=-2.94 EndZ=0
    g1: LineSegment StartX=22.3 StartY=-1.94 StartZ=0 EndX=22.3 EndY=1.45 EndZ=0
    g2: LineSegment StartX=21.3 StartY=2.45 StartZ=0 EndX=12.2 EndY=2.45 EndZ=0
    g3: LineSegment StartX=11.2 StartY=1.45 StartZ=0 EndX=11.2 EndY=-1.94 EndZ=0
    g4: ArcOfCircle CenterX=12.2 CenterY=-1.94 CenterZ=0 NormalX=0 NormalY=0 NormalZ=1 AngleXU=0 Radius=1 StartAngle=3.14159 EndAngle=4.71239
    g5: ArcOfCircle CenterX=21.3 CenterY=-1.94 CenterZ=0 NormalX=0 NormalY=0 NormalZ=1 AngleXU=0 Radius=1 StartAngle=4.71239 EndAngle=6.28319
    g6: ArcOfCircle CenterX=21.3 CenterY=1.45 CenterZ=0 NormalX=0 NormalY=0 NormalZ=1 AngleXU=0 Radius=1 StartAngle=0 EndAngle=1.5708
    g7: ArcOfCircle CenterX=12.2 CenterY=1.45 CenterZ=0 NormalX=0 NormalY=0 NormalZ=1 AngleXU=0 Radius=1 StartAngle=1.5708 EndAngle=3.14159
    g8: GeomPoint [constr] X=11.2 Y=-2.94 Z=0
    g9: GeomPoint [constr] X=22.3 Y=2.45 Z=0
  constraints (24):
    c: Tangent(g0,g4) = -1.5708
    c: Tangent(g0,g5) = -1.5708
    c: Tangent(g1,g5) = -1.5708
    c: Tangent(g1,g6) = -1.5708
    c: Tangent(g2,g6) = -1.5708
    c: Tangent(g2,g7) = -1.5708
    c: Tangent(g3,g7) = -1.5708
    c: Tangent(g3,g4) = -1.5708
    c: Horizontal(g0)
    c: Horizontal(g2)
    c: Vertical(g1)
    c: Vertical(g3)
    c: Equal(g4,g5)
    c: Equal(g5,g6)
    c: Equal(g6,g7)
    c: PointOnObject(g8,g0)
    c: PointOnObject(g8,g3)
    c: PointOnObject(g9,g1)
    c: PointOnObject(g9,g2)
    c: Radius(g5) = 1
    c: DistanceY(g-3,g2) = 1
    c: DistanceX(g3,g-5) = 1
    c: DistanceX(g-6,g1) = 1
    c: DistanceY(g0,g-4) = 1
FEATURE [PartDesign::Pocket] Pocket007
  BaseFeature = -> Fillet015
  Direction = (0,0,1)
  Length = 0.5
  Length2 = 5
  Placement = pos=(0,0,0) rot=(1,0,0;1.5708rad)
  Profile = -> Sketch021
  ReferenceAxis = -> Sketch021 [N_Axis]
  Refine = true
  Suppressed = false
  Type = 0
FEATURE [Sketcher::SketchObject] Sketch031
  ArcFitTolerance = 1e-06
  FullyConstrained = true
  MakeInternals = false
  MapMode = 5
  Placement = pos=(0,3.6e-15,16) rot=(1,0,0;3.14159rad)
  sketch-geometry (2):
    g0: Circle CenterX=16.75 CenterY=0 CenterZ=0 NormalX=0 NormalY=0 NormalZ=1 AngleXU=0 Radius=10
    g1: Circle CenterX=16.75 CenterY=0 CenterZ=0 NormalX=0 NormalY=0 NormalZ=1 AngleXU=0 Radius=10.85
  constraints (4):
    c: Coincident(g0,g-3)
    c: Diameter(g0) = 20
    c: Coincident(g1,g0)
    c: Equal(g-3,g1)
FEATURE [PartDesign::Pocket] Pocket012
  BaseFeature = -> Pocket010
  Direction = (0,0,1)
  Length = 50.5
  Length2 = 5
  Placement = pos=(0,0,0) rot=(1,0,0;1.5708rad)
  Profile = -> Sketch031
  ReferenceAxis = -> Sketch031 [N_Axis]
  Refine = true
  Suppressed = false
  Type = 0
FEATURE [PartDesign::Pocket] Pocket013
  BaseFeature = -> Pocket012
  Direction = (0,-2e-16,-1)
  Length = 5
  Length2 = 5
  Placement = pos=(0,0,0) rot=(1,0,0;1.5708rad)
  Profile = -> Pocket012 [Face29]
  Refine = true
  Suppressed = false
  Type = 0
FEATURE [Sketcher::SketchObject] Sketch032
  ArcFitTolerance = 1e-06
  AttachmentSupport = -> [XZ_Plane001]
  ExternalGeometry = -> [Pocket013]
  FullyConstrained = true
  MakeInternals = false
  MapMode = 5
  Placement = pos=(0,0,0) rot=(1,0,0;1.5708rad)
  sketch-geometry (5):
    g0: LineSegment StartX=19 StartY=64.5 StartZ=0 EndX=19 EndY=63 EndZ=0
    g1: LineSegment StartX=19 StartY=63 StartZ=0 EndX=23 EndY=63 EndZ=0
    g2: LineSegment StartX=23 StartY=63 StartZ=0 EndX=23 EndY=64.5 EndZ=0
    g3: LineSegment StartX=23 StartY=64.5 StartZ=0 EndX=19 EndY=64.5 EndZ=0
    g4: GeomPoint X=21 Y=64.5 Z=0
  constraints (12):
    c: Coincident(g0,g1)
    c: Coincident(g1,g2)
    c: Coincident(g2,g3)
    c: Coincident(g3,g0)
    c: Vertical(g0)
    c: Vertical(g2)
    c: Horizontal(g1)
    c: Horizontal(g3)
    c: Distance(g1,g3) = 1.5
    c: Symmetric(g0,g2,g4)
    c: Symmetric(g-3,g-3,g4)
    c: DistanceX(g0,g2) = 4
FEATURE [PartDesign::Pocket] Pocket014
  BaseFeature = -> Pocket013
  Direction = (0,1,-2e-16)
  Length = 10
  Length2 = 5
  Placement = pos=(0,0,0) rot=(1,0,0;1.5708rad)
  Profile = -> Sketch032
  ReferenceAxis = -> Sketch032 [N_Axis]
  Refine = true
  Reversed = true
  Suppressed = false
  Type = 0
FEATURE [PartDesign::Pad] Pad005
  BaseFeature = -> Pocket014
  Direction = (1,0,0)
  Length = 0.5
  Length2 = 10
  Placement = pos=(0,0,0) rot=(1,0,0;1.5708rad)
  Profile = -> Pocket014 [Face25]
  Refine = true
  Suppressed = false
  Type = 0
FEATURE [Sketcher::SketchObject] Sketch033
  ArcFitTolerance = 1e-06
  AttachmentOffset = pos=(0,0,-5) rot=(0,0,1;0rad)
  AttachmentSupport = -> [XZ_Plane001]
  ExternalGeometry = -> [Pad005]
  FullyConstrained = true
  MakeInternals = false
  MapMode = 5
  Placement = pos=(0,5,-1.1e-15) rot=(1,0,0;1.5708rad)
  sketch-geometry (4):
    g0: LineSegment StartX=11.25 StartY=63.5 StartZ=0 EndX=13.25 EndY=63.5 EndZ=0
    g1: LineSegment StartX=13.25 StartY=63.5 StartZ=0 EndX=13.25 EndY=64.5 EndZ=0
    g2: LineSegment StartX=13.25 StartY=64.5 StartZ=0 EndX=11.25 EndY=64.5 EndZ=0
    g3: LineSegment StartX=11.25 StartY=64.5 StartZ=0 EndX=11.25 EndY=63.5 EndZ=0
  constraints (12):
    c: Coincident(g0,g1)
    c: Coincident(g1,g2)
    c: Coincident(g2,g3)
    c: Coincident(g3,g0)
    c: Horizontal(g0)
    c: Horizontal(g2)
    c: Vertical(g1)
    c: Vertical(g3)
    c: Distance(g1,g3) = 2
    c: Distance(g0,g2) = 1
    c: PointOnObject(g0,g-3)
    c: DistanceX(g-3,g0) = 1
FEATURE [PartDesign::Pocket] Pocket015
  BaseFeature = -> Pad005
  Direction = (0,1,-2e-16)
  Length = 15
  Length2 = 5
  Placement = pos=(0,0,0) rot=(1,0,0;1.5708rad)
  Profile = -> Sketch033
  ReferenceAxis = -> Sketch033 [N_Axis]
  Refine = true
  Reversed = true
  Suppressed = false
  Type = 0
FEATURE [PartDesign::Pad] Pad006
  BaseFeature = -> Pocket015
  Direction = (0,0,-1)
  Length = 24.5
  Length2 = 10
  Placement = pos=(0,0,0) rot=(1,0,0;1.5708rad)
  Profile = -> Pocket015 [Face38]
  Refine = true
  Suppressed = false
  Type = 0
FEATURE [Sketcher::SketchObject] Sketch034
  ArcFitTolerance = 1e-06
  AttachmentSupport = -> [Pad006]
  ExternalGeometry = -> [Pad006]
  FullyConstrained = true
  MakeInternals = false
  MapMode = 5
  Placement = pos=(0,5e-15,16) rot=(1,0,0;3.14159rad)
  sketch-geometry (10):
    g0: LineSegment StartX=6.76251 StartY=0.5 StartZ=0 EndX=9.76251 EndY=0.5 EndZ=0
    g1: LineSegment StartX=9.76251 StartY=0.5 StartZ=0 EndX=9.76251 EndY=-1.8 EndZ=0
    g2: LineSegment StartX=9.76251 StartY=-1.8 StartZ=0 EndX=12.15 EndY=-1.8 EndZ=0
    g3: LineSegment StartX=12.15 StartY=-1.8 StartZ=0 EndX=12.15 EndY=-2 EndZ=0
    g4: LineSegment StartX=12.15 StartY=-2 StartZ=0 EndX=21.35 EndY=-2 EndZ=0
    g5: LineSegment StartX=21.35 StartY=-2 StartZ=0 EndX=21.35 EndY=-1.8 EndZ=0
    g6: LineSegment StartX=21.35 StartY=-1.8 StartZ=0 EndX=23.7375 EndY=-1.8 EndZ=0
    g7: LineSegment StartX=23.7375 StartY=-1.8 StartZ=0 EndX=23.7375 EndY=0.5 EndZ=0
    g8: LineSegment StartX=23.7375 StartY=0.5 StartZ=0 EndX=26.7375 EndY=0.5 EndZ=0
    g9: ArcOfCircle CenterX=16.75 CenterY=2.21e-14 CenterZ=0 NormalX=0 NormalY=0 NormalZ=1 AngleXU=0 Radius=10 StartAngle=0.0500209 EndAngle=3.09157
  constraints (31):
    c: PointOnObject(g0,g-3)
    c: Horizontal(g0)
    c: Coincident(g0,g1)
    c: Vertical(g1)
    c: Coincident(g1,g2)
    c: Horizontal(g2)
    c: Coincident(g2,g3)
    c: Vertical(g3)
    c: Coincident(g3,g4)
    c: Horizontal(g4)
    c: Coincident(g4,g5)
    c: Vertical(g5)
    c: Coincident(g5,g6)
    c: Horizontal(g6)
    c: Coincident(g6,g7)
    c: Vertical(g7)
    c: Coincident(g7,g8)
    c: PointOnObject(g8,g-3)
    c: Horizontal(g8)
    c: Coincident(g9,g0)
    c: Coincident(g9,g8)
    c: Equal(g9,g-3)
    c: Equal(g0,g8)
    c: Equal(g7,g1)
    c: Equal(g2,g6)
    c: Equal(g5,g3)
    c: DistanceX(g8,g8) = 3
    c: DistanceY(g7,g7) = 2.3
    c: DistanceY(g5,g5) = 0.2
    c: DistanceX(g4,g4) = 9.2
    c: DistanceY(g-1,g8) = 0.5
FEATURE [PartDesign::Pocket] Pocket016
  BaseFeature = -> Pad006
  Direction = (0,0,1)
  Length = 24
  Length2 = 5
  Placement = pos=(0,0,0) rot=(1,0,0;1.5708rad)
  Profile = -> Sketch034
  ReferenceAxis = -> Sketch034 [N_Axis]
  Refine = true
  Suppressed = false
  Type = 0
FEATURE [Sketcher::SketchObject] Sketch035
  ArcFitTolerance = 1e-06
  AttachmentSupport = -> [Pocket016]
  ExternalGeometry = -> [Pocket016]
  FullyConstrained = true
  MakeInternals = false
  MapMode = 5
  Placement = pos=(0,0,40) rot=(1,0,0;3.14159rad)
  sketch-geometry (4):
    g0: LineSegment StartX=23.7375 StartY=0.5 StartZ=0 EndX=9.76251 EndY=0.5 EndZ=0
    g1: LineSegment StartX=9.76251 StartY=0.5 StartZ=0 EndX=9.76251 EndY=-2 EndZ=0
    g2: LineSegment StartX=9.76251 StartY=-2 StartZ=0 EndX=23.7375 EndY=-2 EndZ=0
    g3: LineSegment StartX=23.7375 StartY=-2 StartZ=0 EndX=23.7375 EndY=0.5 EndZ=0
  constraints (11):
    c: Coincident(g0,g1)
    c: Coincident(g2,g3)
    c: Coincident(g3,g0)
    c: Horizontal(g0)
    c: Horizontal(g2)
    c: Vertical(g1)
    c: Vertical(g3)
    c: Coincident(g0,g-4)
    c: Coincident(g2,g1)
    c: Vertical(g1,g-5)
    c: PointOnObject(g-6,g2)
FEATURE [PartDesign::Pad] Pad007
  BaseFeature = -> Pocket016
  Direction = (0,0,-1)
  Length = 5
  Length2 = 10
  Placement = pos=(0,0,0) rot=(1,0,0;1.5708rad)
  Profile = -> Sketch035
  ReferenceAxis = -> Sketch035 [N_Axis]
  Refine = true
  Suppressed = false
  Type = 0
FEATURE [PartDesign::Pad] Pad008
  BaseFeature = -> Pad007
  Direction = (0,0,-1)
  Length = 5
  Length2 = 10
  Placement = pos=(0,0,0) rot=(1,0,0;1.5708rad)
  Profile = -> Sketch035
  ReferenceAxis = -> Sketch035 [N_Axis]
  Refine = true
  Suppressed = false
  Type = 0
FEATURE [Sketcher::SketchObject] Sketch036
  ArcFitTolerance = 1e-06
  AttachmentSupport = -> [Pad008]
  ExternalGeometry = -> [Pad008]
  FullyConstrained = true
  MakeInternals = false
  MapMode = 5
  Placement = pos=(0,5e-15,16) rot=(1,0,0;3.14159rad)
  sketch-geometry (8):
    g0: LineSegment StartX=9.76251 StartY=-1.8 StartZ=0 EndX=11.7625 EndY=-1.8 EndZ=0
    g1: LineSegment StartX=11.7625 StartY=-1.8 StartZ=0 EndX=11.7625 EndY=0 EndZ=0
    g2: LineSegment StartX=11.7625 StartY=0 StartZ=0 EndX=9.76251 EndY=0 EndZ=0
    g3: LineSegment StartX=9.76251 StartY=0 StartZ=0 EndX=9.76251 EndY=-1.8 EndZ=0
    g4: LineSegment StartX=23.7375 StartY=-1.8 StartZ=0 EndX=23.7375 EndY=2e-16 EndZ=0
    g5: LineSegment StartX=23.7375 StartY=2e-16 StartZ=0 EndX=21.7375 EndY=2e-16 EndZ=0
    g6: LineSegment StartX=21.7375 StartY=2e-16 StartZ=0 EndX=21.7375 EndY=-1.8 EndZ=0
    g7: LineSegment StartX=21.7375 StartY=-1.8 StartZ=0 EndX=23.7375 EndY=-1.8 EndZ=0
  constraints (22):
    c: Coincident(g0,g1)
    c: Coincident(g1,g2)
    c: Coincident(g2,g3)
    c: Coincident(g3,g0)
    c: Horizontal(g0)
    c: Horizontal(g2)
    c: Vertical(g1)
    c: Vertical(g3)
    c: Distance(g1,g3) = 2
    c: Distance(g0,g2) = 1.8
    c: Coincident(g0,g-4)
    c: Coincident(g4,g5)
    c: Coincident(g5,g6)
    c: Coincident(g6,g7)
    c: Coincident(g7,g4)
    c: Vertical(g4)
    c: Vertical(g6)
    c: Horizontal(g5)
    c: Horizontal(g7)
    c: Coincident(g4,g-3)
    c: Equal(g6,g1)
    c: Equal(g5,g2)
FEATURE [PartDesign::Pad] Pad009
  BaseFeature = -> Pad008
  Direction = (0,0,-1)
  Length = 5
  Length2 = 10
  Placement = pos=(0,0,0) rot=(1,0,0;1.5708rad)
  Profile = -> Sketch036
  ReferenceAxis = -> Sketch036 [N_Axis]
  Refine = true
  Reversed = true
  Suppressed = false
  Type = 0
FEATURE [PartDesign::Pocket] Pocket017
  BaseFeature = -> Pad009
  Direction = (0,-2e-16,1)
  Length = 1
  Length2 = 5
  Placement = pos=(0,0,0) rot=(1,0,0;1.5708rad)
  Profile = -> Pad009 [Face52]
  Refine = true
  Suppressed = false
  Type = 0
FEATURE [Sketcher::SketchObject] Sketch038
  ArcFitTolerance = 1e-06
  AttachmentOffset = pos=(0,0,1) rot=(0,0,1;0rad)
  AttachmentSupport = -> [Pocket007]
  ExternalGeometry = -> [Pocket007]
  FullyConstrained = true
  MakeInternals = false
  MapMode = 5
  Placement = pos=(0,0,41) rot=(0,0,1;3.14159rad)
  sketch-geometry (1):
    g0: Circle CenterX=-16.75 CenterY=0 CenterZ=0 NormalX=0 NormalY=0 NormalZ=1 AngleXU=0 Radius=11
  constraints (2):
    c: Coincident(g0,g-3)
    c: Equal(g-3,g0)
FEATURE [PartDesign::Pocket] Pocket018
  BaseFeature = -> Pocket007
  Direction = (0,0,-1)
  Length = 25
  Length2 = 5
  Placement = pos=(0,0,0) rot=(1,0,0;1.5708rad)
  Profile = -> Sketch038
  ReferenceAxis = -> Sketch038 [N_Axis]
  Refine = true
  Suppressed = false
  Type = 0
FEATURE [Sketcher::SketchObject] Sketch039
  ArcFitTolerance = 1e-06
  AttachmentSupport = -> [Pocket017]
  ExternalGeometry = -> [Pocket017]
  FullyConstrained = true
  MakeInternals = false
  MapMode = 5
  Placement = pos=(0,0,35) rot=(1,0,0;3.14159rad)
  sketch-geometry (4):
    g0: LineSegment StartX=21.35 StartY=-2 StartZ=0 EndX=21.35 EndY=-1.8 EndZ=0
    g1: LineSegment StartX=21.35 StartY=-1.8 StartZ=0 EndX=12.15 EndY=-1.8 EndZ=0
    g2: LineSegment StartX=12.15 StartY=-1.8 StartZ=0 EndX=12.15 EndY=-2 EndZ=0
    g3: LineSegment StartX=12.15 StartY=-2 StartZ=0 EndX=21.35 EndY=-2 EndZ=0
  constraints (10):
    c: Coincident(g0,g1)
    c: Coincident(g1,g2)
    c: Coincident(g2,g3)
    c: Coincident(g3,g0)
    c: Vertical(g0)
    c: Vertical(g2)
    c: Horizontal(g1)
    c: Horizontal(g3)
    c: Coincident(g0,g-4)
    c: Coincident(g1,g-3)
FEATURE [PartDesign::Pad] Pad011
  BaseFeature = -> Pocket017
  Direction = (0,0,-1)
  Length = 11
  Length2 = 10
  Placement = pos=(0,0,0) rot=(1,0,0;1.5708rad)
  Profile = -> Sketch039
  ReferenceAxis = -> Sketch039 [N_Axis]
  Refine = true
  Suppressed = false
  Type = 0
FEATURE [PartDesign::Fillet] Fillet019
  Base = -> Pad011 [Edge125,Edge127]
  BaseFeature = -> Pad011
  Placement = pos=(0,0,0) rot=(1,0,0;1.5708rad)
  Radius = 0.125
  Refine = true
  SupportTransform = false
  Suppressed = false
  UseAllEdges = false
FEATURE [PartDesign::Fillet] Fillet020
  Base = -> Fillet019 [Edge33,Edge31,Edge19,Edge30]
  BaseFeature = -> Fillet019
  Placement = pos=(0,0,0) rot=(1,0,0;1.5708rad)
  Radius = 0.0625
  Refine = true
  SupportTransform = false
  Suppressed = false
  UseAllEdges = false
FEATURE [PartDesign::Fillet] Fillet021
  Base = -> Fillet020 [Edge77,Edge40,Edge50,Edge80,Edge49,Edge81]
  BaseFeature = -> Fillet020
  Placement = pos=(0,0,0) rot=(1,0,0;1.5708rad)
  Radius = 0.5
  Refine = true
  SupportTransform = false
  Suppressed = false
  UseAllEdges = false
FEATURE [PartDesign::Fillet] Fillet022
  Base = -> Fillet021 [Edge12,Edge60]
  BaseFeature = -> Fillet021
  Placement = pos=(0,0,0) rot=(1,0,0;1.5708rad)
  Radius = 0.125
  Refine = true
  SupportTransform = false
  Suppressed = false
  UseAllEdges = false
FEATURE [PartDesign::Fillet] Fillet023
  Base = -> Fillet022 [Edge98]
  BaseFeature = -> Fillet022
  Placement = pos=(0,0,0) rot=(1,0,0;1.5708rad)
  Radius = 0.25
  Refine = true
  SupportTransform = false
  Suppressed = false
  UseAllEdges = false
FEATURE [PartDesign::Fillet] Fillet024
  Base = -> Fillet023 [Edge176,Edge177]
  BaseFeature = -> Fillet023
  Placement = pos=(0,0,0) rot=(1,0,0;1.5708rad)
  Radius = 1
  Refine = true
  SupportTransform = false
  Suppressed = false
  UseAllEdges = false
FEATURE [PartDesign::Fillet] Fillet025
  Base = -> Fillet024 [Edge8,Edge53]
  BaseFeature = -> Fillet024
  Placement = pos=(0,0,0) rot=(1,0,0;1.5708rad)
  Radius = 1
  Refine = true
  SupportTransform = false
  Suppressed = false
  UseAllEdges = false
FEATURE [PartDesign::Fillet] Fillet026
  Base = -> Fillet025 [Edge10]
  BaseFeature = -> Fillet025
  Placement = pos=(0,0,0) rot=(1,0,0;1.5708rad)
  Radius = 0.25
  Refine = true
  SupportTransform = false
  Suppressed = false
  UseAllEdges = false
FEATURE [PartDesign::Chamfer] Chamfer
  Angle = 45
  Base = -> Fillet026 [Edge146,Edge154]
  BaseFeature = -> Fillet026
  ChamferType = 1
  FlipDirection = false
  Placement = pos=(0,0,0) rot=(1,0,0;1.5708rad)
  Refine = true
  Size = 1
  Size2 = 3
  SupportTransform = false
  Suppressed = false
  UseAllEdges = false
FEATURE [PartDesign::Fillet] Fillet027
  Base = -> Chamfer [Edge43,Edge6,Edge78]
  BaseFeature = -> Chamfer
  Placement = pos=(0,0,0) rot=(1,0,0;1.5708rad)
  Radius = 0.25
  Refine = true
  SupportTransform = false
  Suppressed = false
  UseAllEdges = false
FEATURE [PartDesign::Fillet] Fillet028
  Base = -> Fillet027 [Edge65,Edge68]
  BaseFeature = -> Fillet027
  Placement = pos=(0,0,0) rot=(1,0,0;1.5708rad)
  Radius = 1
  Refine = true
  SupportTransform = false
  Suppressed = false
  UseAllEdges = false
FEATURE [PartDesign::Fillet] Fillet029
  Base = -> Fillet028 [Edge3]
  BaseFeature = -> Fillet028
  Placement = pos=(0,0,0) rot=(1,0,0;1.5708rad)
  Radius = 0.25
  Refine = true
  SupportTransform = false
  Suppressed = false
  UseAllEdges = false
FEATURE [PartDesign::Fillet] Fillet030
  Base = -> Fillet029 [Edge52,Edge10,Edge8,Edge14,Edge55,Edge63]
  BaseFeature = -> Fillet029
  Placement = pos=(0,0,0) rot=(1,0,0;1.5708rad)
  Radius = 0.25
  Refine = true
  SupportTransform = false
  Suppressed = false
  UseAllEdges = false
FEATURE [PartDesign::Fillet] Fillet031
  Base = -> Fillet030 [Edge170,Edge272]
  BaseFeature = -> Fillet030
  Placement = pos=(0,0,0) rot=(1,0,0;1.5708rad)
  Radius = 5
  Refine = true
  SupportTransform = false
  Suppressed = false
  UseAllEdges = false
FEATURE [PartDesign::Fillet] Fillet032
  Base = -> Fillet031 [Edge195,Edge17]
  BaseFeature = -> Fillet031
  Placement = pos=(0,0,0) rot=(1,0,0;1.5708rad)
  Radius = 0.125
  Refine = true
  SupportTransform = false
  Suppressed = false
  UseAllEdges = false
FEATURE [PartDesign::Fillet] Fillet033
  Base = -> Fillet032 [Edge109,Edge23]
  BaseFeature = -> Fillet032
  Placement = pos=(0,0,0) rot=(1,0,0;1.5708rad)
  Radius = 0.25
  Refine = true
  SupportTransform = false
  Suppressed = false
  UseAllEdges = false
FEATURE [PartDesign::Pocket] Pocket019
  BaseFeature = -> Fillet033
  Direction = (3e-16,1,-2.3e-15)
  Length = 0.5
  Length2 = 5
  Placement = pos=(0,0,0) rot=(1,0,0;1.5708rad)
  Profile = -> Fillet033 [Face12]
  Refine = true
  Suppressed = false
  Type = 0
FEATURE [PartDesign::Fillet] Fillet034
  Base = -> Pocket019 [Edge354,Edge358]
  BaseFeature = -> Pocket019
  Placement = pos=(0,0,0) rot=(1,0,0;1.5708rad)
  Radius = 0.125
  Refine = true
  SupportTransform = false
  Suppressed = false
  UseAllEdges = false
FEATURE [PartDesign::Fillet] Fillet035
  Base = -> Fillet034 [Edge101,Edge99,Edge96,Edge97]
  BaseFeature = -> Fillet034
  Placement = pos=(0,0,0) rot=(1,0,0;1.5708rad)
  Radius = 0.25
  Refine = true
  SupportTransform = false
  Suppressed = false
  UseAllEdges = false
FEATURE [PartDesign::Fillet] Fillet036
  Base = -> Fillet035 [Edge1]
  BaseFeature = -> Fillet035
  Placement = pos=(0,0,0) rot=(1,0,0;1.5708rad)
  Radius = 0.25
  Refine = true
  SupportTransform = false
  Suppressed = false
  UseAllEdges = false
FEATURE [PartDesign::Fillet] Fillet037
  Base = -> Fillet036 [Edge252]
  BaseFeature = -> Fillet036
  Placement = pos=(0,0,0) rot=(1,0,0;1.5708rad)
  Radius = 0.25
  Refine = true
  SupportTransform = false
  Suppressed = false
  UseAllEdges = false
FEATURE [PartDesign::Fillet] Fillet038
  Base = -> Fillet037 [Edge363]
  BaseFeature = -> Fillet037
  Placement = pos=(0,0,0) rot=(1,0,0;1.5708rad)
  Radius = 0.5
  Refine = true
  SupportTransform = false
  Suppressed = false
  UseAllEdges = false
FEATURE [PartDesign::Fillet] Fillet039
  Base = -> Fillet038 [Edge14,Edge23]
  BaseFeature = -> Fillet038
  Placement = pos=(0,0,0) rot=(1,0,0;1.5708rad)
  Radius = 2
  Refine = true
  SupportTransform = false
  Suppressed = false
  UseAllEdges = false
FEATURE [PartDesign::Fillet] Fillet040
  Base = -> Fillet039 [Edge35]
  BaseFeature = -> Fillet039
  Placement = pos=(0,0,0) rot=(1,0,0;1.5708rad)
  Radius = 0.125
  Refine = true
  SupportTransform = false
  Suppressed = false
  UseAllEdges = false
FEATURE [PartDesign::Fillet] Fillet041
  Base = -> Fillet040 [Edge106]
  BaseFeature = -> Fillet040
  Placement = pos=(0,0,0) rot=(1,0,0;1.5708rad)
  Radius = 0.25
  Refine = true
  SupportTransform = false
  Suppressed = false
  UseAllEdges = false
FEATURE [PartDesign::Fillet] Fillet042
  Base = -> Fillet041 [Edge88,Edge12]
  BaseFeature = -> Fillet041
  Placement = pos=(0,0,0) rot=(1,0,0;1.5708rad)
  Radius = 0.25
  Refine = true
  SupportTransform = false
  Suppressed = false
  UseAllEdges = false
FEATURE [PartDesign::Fillet] Fillet043
  Base = -> Fillet042 [Edge203,Edge197,Edge167,Edge166]
  BaseFeature = -> Fillet042
  Placement = pos=(0,0,0) rot=(1,0,0;1.5708rad)
  Radius = 0.25
  Refine = true
  SupportTransform = false
  Suppressed = false
  UseAllEdges = false
FEATURE [PartDesign::Fillet] Fillet044
  Base = -> Fillet043 [Edge20]
  BaseFeature = -> Fillet043
  Placement = pos=(0,0,0) rot=(1,0,0;1.5708rad)
  Radius = 0.0625
  Refine = true
  SupportTransform = false
  Suppressed = false
  UseAllEdges = false
FEATURE [Sketcher::SketchObject] Sketch040
  ArcFitTolerance = 1e-06
  AttachmentSupport = -> [Fillet044]
  FullyConstrained = true
  MakeInternals = false
  MapMode = 5
  Placement = pos=(0,1.8,0) rot=(1,0,0;1.5708rad)
  sketch-geometry (4):
    g0: LineSegment StartX=18.4 StartY=30.2 StartZ=0 EndX=18.4 EndY=33.2 EndZ=0
    g1: LineSegment StartX=18.4 StartY=33.2 StartZ=0 EndX=15.4 EndY=33.2 EndZ=0
    g2: LineSegment StartX=15.4 StartY=33.2 StartZ=0 EndX=15.4 EndY=30.2 EndZ=0
    g3: LineSegment StartX=15.4 StartY=30.2 StartZ=0 EndX=18.4 EndY=30.2 EndZ=0
  constraints (12):
    c: Coincident(g0,g1)
    c: Coincident(g1,g2)
    c: Coincident(g2,g3)
    c: Coincident(g3,g0)
    c: Vertical(g0)
    c: Vertical(g2)
    c: Horizontal(g1)
    c: Horizontal(g3)
    c: Distance(g0,g2) = 3
    c: Distance(g1,g3) = 3
    c: DistanceY(g-1,g2) = 30.2
    c: DistanceX(g-1,g2) = 15.4
FEATURE [PartDesign::Pocket] Pocket020
  BaseFeature = -> Fillet044
  Direction = (0,1,-2e-16)
  Length = 9
  Length2 = 5
  Placement = pos=(0,0,0) rot=(1,0,0;1.5708rad)
  Profile = -> Sketch040
  ReferenceAxis = -> Sketch040 [N_Axis]
  Refine = true
  Suppressed = false
  Type = 0
FEATURE [Sketcher::SketchObject] Sketch041
  ArcFitTolerance = 1e-06
  AttachmentSupport = -> [XZ_Plane]
  FullyConstrained = true
  MakeInternals = false
  MapMode = 5
  Placement = pos=(0,0,0) rot=(1,0,0;1.5708rad)
  sketch-geometry (4):
    g0: LineSegment StartX=18.4 StartY=30.2 StartZ=0 EndX=18.4 EndY=33.2 EndZ=0
    g1: LineSegment StartX=18.4 StartY=33.2 StartZ=0 EndX=15.4 EndY=33.2 EndZ=0
    g2: LineSegment StartX=15.4 StartY=33.2 StartZ=0 EndX=15.4 EndY=30.2 EndZ=0
    g3: LineSegment StartX=15.4 StartY=30.2 StartZ=0 EndX=18.4 EndY=30.2 EndZ=0
  constraints (12):
    c: Coincident(g0,g1)
    c: Coincident(g1,g2)
    c: Coincident(g2,g3)
    c: Coincident(g3,g0)
    c: Vertical(g0)
    c: Vertical(g2)
    c: Horizontal(g1)
    c: Horizontal(g3)
    c: Distance(g0,g2) = 3
    c: Distance(g1,g3) = 3
    c: DistanceY(g-1,g2) = 30.2
    c: DistanceX(g-1,g2) = 15.4
FEATURE [PartDesign::Pocket] Pocket021
  BaseFeature = -> Pocket018
  Direction = (0,1,-2e-16)
  Length = 12.5
  Length2 = 5
  Placement = pos=(0,0,0) rot=(1,0,0;1.5708rad)
  Profile = -> Sketch041
  ReferenceAxis = -> Sketch041 [N_Axis]
  Refine = true
  Suppressed = false
  Type = 0
FEATURE [PartDesign::Fillet] Fillet045
  Base = -> Pocket021 [Edge53,Edge55,Edge51,Edge49]
  BaseFeature = -> Pocket021
  Placement = pos=(0,0,0) rot=(1,0,0;1.5708rad)
  Radius = 1
  Refine = true
  SupportTransform = false
  Suppressed = false
  UseAllEdges = false
FEATURE [PartDesign::Pad] Pad012
  BaseFeature = -> Fillet045
  Direction = (0,1e-16,1)
  Length = 0.5
  Length2 = 10
  Placement = pos=(0,0,0) rot=(1,0,0;1.5708rad)
  Profile = -> Fillet045 [Face11]
  Refine = true
  Suppressed = false
  Type = 0
FEATURE [PartDesign::Pocket] Pocket022
  BaseFeature = -> Pad012
  Direction = (0,0,1)
  Length = 0.5
  Length2 = 5
  Placement = pos=(0,0,0) rot=(1,0,0;1.5708rad)
  Profile = -> Pad012 [Face51]
  Refine = true
  Suppressed = false
  Type = 0
FEATURE [PartDesign::Fillet] Fillet046
  Base = -> Pocket022 [Edge3]
  BaseFeature = -> Pocket022
  Placement = pos=(0,0,0) rot=(1,0,0;1.5708rad)
  Radius = 2
  Refine = true
  SupportTransform = false
  Suppressed = false
  UseAllEdges = false
FEATURE [PartDesign::Fillet] Fillet047
  Base = -> Fillet046 [Edge170,Edge132]
  BaseFeature = -> Fillet046
  Placement = pos=(0,0,0) rot=(1,0,0;1.5708rad)
  Radius = 0.4
  Refine = true
  SupportTransform = false
  Suppressed = false
  UseAllEdges = false
FEATURE [PartDesign::Fillet] Fillet048
  Base = -> Fillet047 [Edge14]
  BaseFeature = -> Fillet047
  Placement = pos=(0,0,0) rot=(1,0,0;1.5708rad)
  Radius = 0.125
  Refine = true
  SupportTransform = false
  Suppressed = false
  UseAllEdges = false
FEATURE [Sketcher::SketchObject] Sketch042
  ArcFitTolerance = 1e-06
  AttachmentSupport = -> [XZ_Plane]
  ExternalGeometry = -> [Fillet048]
  FullyConstrained = true
  MakeInternals = false
  MapMode = 5
  Placement = pos=(0,0,0) rot=(1,0,0;1.5708rad)
  sketch-geometry (4):
    g0: LineSegment StartX=27.75 StartY=70.5 StartZ=0 EndX=27.5 EndY=70.5 EndZ=0
    g1: LineSegment StartX=27.5 StartY=70.5 StartZ=0 EndX=27.5 EndY=69.5 EndZ=0
    g2: LineSegment StartX=27.5 StartY=69.5 StartZ=0 EndX=27.75 EndY=69.5 EndZ=0
    g3: LineSegment StartX=27.75 StartY=69.5 StartZ=0 EndX=27.75 EndY=70.5 EndZ=0
  constraints (12):
    c: Coincident(g0,g1)
    c: Coincident(g1,g2)
    c: Coincident(g2,g3)
    c: Coincident(g3,g0)
    c: Horizontal(g0)
    c: Horizontal(g2)
    c: Vertical(g1)
    c: Vertical(g3)
    c: DistanceY(g-3,g2) = 51
    c: DistanceY(g3,g3) = 1
    c: DistanceX(g0,g0) = 0.25
    c: Vertical(g2,g-3)
FEATURE [PartDesign::Pad] Pad013
  BaseFeature = -> Fillet048
  Direction = (0,-1,2e-16)
  Length = 10
  Length2 = 10
  Midplane = true
  Placement = pos=(0,0,0) rot=(1,0,0;1.5708rad)
  Profile = -> Sketch042
  ReferenceAxis = -> Sketch042 [N_Axis]
  Refine = true
  Suppressed = false
  Type = 0
FEATURE [Sketcher::SketchObject] Sketch043
  ArcFitTolerance = 1e-06
  AttachmentSupport = -> [XZ_Plane001]
  FullyConstrained = true
  MakeInternals = false
  MapMode = 5
  Placement = pos=(0,0,0) rot=(1,0,0;1.5708rad)
  sketch-geometry (4):
    g0: LineSegment StartX=27.7 StartY=70.375 StartZ=0 EndX=27.2 EndY=70.375 EndZ=0
    g1: LineSegment StartX=27.2 StartY=70.375 StartZ=0 EndX=27.2 EndY=68.75 EndZ=0
    g2: LineSegment StartX=27.2 StartY=68.75 StartZ=0 EndX=27.7 EndY=68.75 EndZ=0
    g3: LineSegment StartX=27.7 StartY=68.75 StartZ=0 EndX=27.7 EndY=70.375 EndZ=0
  constraints (12):
    c: Coincident(g0,g1)
    c: Coincident(g1,g2)
    c: Coincident(g2,g3)
    c: Coincident(g3,g0)
    c: Horizontal(g0)
    c: Horizontal(g2)
    c: Vertical(g1)
    c: Vertical(g3)
    c: Distance(g1,g3) = 0.5
    c: Distance(g0,g2) = 1.625
    c: DistanceY(g-1,g2) = 68.75
    c: DistanceX(g-1,g2) = 27.7
FEATURE [PartDesign::Pocket] Pocket023
  BaseFeature = -> Pocket020
  Direction = (0,1,-2e-16)
  Length = 10
  Length2 = 5
  Midplane = true
  Placement = pos=(0,0,0) rot=(1,0,0;1.5708rad)
  Profile = -> Sketch043
  ReferenceAxis = -> Sketch043 [N_Axis]
  Refine = true
  Suppressed = false
  Type = 0
FEATURE [PartDesign::Fillet] Fillet049
  Base = -> Pocket023 [Edge692,Edge691]
  BaseFeature = -> Pocket023
  Placement = pos=(0,0,0) rot=(1,0,0;1.5708rad)
  Radius = 0.3
  Refine = true
  SupportTransform = false
  Suppressed = false
  UseAllEdges = false
FEATURE [PartDesign::Fillet] Fillet050
  Base = -> Fillet049 [Edge7,Edge1]
  BaseFeature = -> Fillet049
  Placement = pos=(0,0,0) rot=(1,0,0;1.5708rad)
  Radius = 0.5
  Refine = true
  SupportTransform = false
  Suppressed = false
  UseAllEdges = false
FEATURE [PartDesign::Body] Body001  label="Core"
  AllowCompound = true
  Group = -> [Sketch003,Sketch004,Revolution,Pad001,Sketch012,Pocket004,Sketch013,Sketch015,Pad002,Pocket005,Sketch016,Pocket006,Sketch017,Sketch018,SubtractivePipe,SubtractiveLoft,Sketch019,Pad003,Sketch024,Revolution001,Sketch026,SubtractiveLoft001,Sketch027,Sketch028,Pad004,Pocket008,Pocket009,Sketch029,Pocket010,Sketch031,Pocket012,Pocket013,Sketch032,Pocket014,Pad005,Sketch033,Pocket015,Pad006,Sketch034,+43 more]
  Origin = -> Origin001
  Placement = pos=(0,0,0.5) rot=(0,0,1;0rad)
  Tip = -> Fillet050
FEATURE [PartDesign::Fillet] Fillet051
  Base = -> Pad013 [Edge162,Edge163]
  BaseFeature = -> Pad013
  Placement = pos=(0,0,0) rot=(1,0,0;1.5708rad)
  Radius = 0.2
  Refine = true
  SupportTransform = false
  Suppressed = false
  UseAllEdges = false
FEATURE [PartDesign::Fillet] Fillet052
  Base = -> Fillet051 [Edge1]
  BaseFeature = -> Fillet051
  Placement = pos=(0,0,0) rot=(1,0,0;1.5708rad)
  Radius = 0.35
  Refine = true
  SupportTransform = false
  Suppressed = false
  UseAllEdges = false
FEATURE [Sketcher::SketchObject] Sketch044
  ArcFitTolerance = 1e-06
  AttachmentOffset = pos=(-2.5,3,0) rot=(0,0,1;0rad)
  AttachmentSupport = -> [Fillet052]
  FullyConstrained = false
  MakeInternals = false
  MapMode = 5
  Placement = pos=(-2.5,13.5,-3) rot=(-1,0,0;1.5708rad)
  sketch-geometry (22):
    g0: GeomPoint [constr] X=26.4662 Y=-41.9422 Z=0
    g1: GeomPoint [constr] X=11.6687 Y=-27.1448 Z=0
    g2: LineSegment StartX=25.3 StartY=-41.7 StartZ=0 EndX=19.529 EndY=-41.7 EndZ=0
    g3: LineSegment StartX=25.3 StartY=-41.7 StartZ=0 EndX=25.3 EndY=-33.1915 EndZ=0
    g4: LineSegment StartX=25.3 StartY=-33.1915 StartZ=0 EndX=27.6231 EndY=-33.6515 EndZ=0
    g5: LineSegment StartX=27.6231 StartY=-33.6515 StartZ=0 EndX=24.0792 EndY=-28.4563 EndZ=0
    g6: LineSegment StartX=24.0792 StartY=-28.4563 StartZ=0 EndX=20.5353 EndY=-33.6515 EndZ=0
    g7: LineSegment StartX=20.5353 StartY=-33.6515 StartZ=0 EndX=22.8584 EndY=-33.1915 EndZ=0
    g8: LineSegment StartX=22.8584 StartY=-33.1915 StartZ=0 EndX=22.8584 EndY=-39.2584 EndZ=0
    g9: LineSegment StartX=22.8584 StartY=-39.2584 StartZ=0 EndX=19.1591 EndY=-39.2584 EndZ=0
    g10: LineSegment StartX=21.1567 StartY=-30.38 StartZ=0 EndX=22.8222 EndY=-27.9384 EndZ=0
    g11: LineSegment StartX=22.8222 StartY=-27.9384 StartZ=0 EndX=19.529 EndY=-27.9384 EndZ=0
    g12: LineSegment StartX=21.1567 StartY=-30.38 StartZ=0 EndX=19.1591 EndY=-30.38 EndZ=0
    g13: ArcOfCircle CenterX=19.8989 CenterY=-34.8192 CenterZ=0 NormalX=0 NormalY=0 NormalZ=1 AngleXU=0 Radius=4.50047 StartAngle=1.73594 EndAngle=4.54724
    g14: ArcOfCircle CenterX=19.8989 CenterY=-34.8192 CenterZ=0 NormalX=0 NormalY=0 NormalZ=1 AngleXU=0 Radius=6.89075 StartAngle=1.62451 EndAngle=4.65868
    g15: GeomPoint X=24.0792 Y=-40.4792 Z=0
    g16: LineSegment [constr] StartX=19.1591 StartY=-35.1151 StartZ=0 EndX=20.583 EndY=-36.3529 EndZ=0
    g17: LineSegment [constr] StartX=20.583 StartY=-36.3529 StartZ=0 EndX=21.6236 EndY=-35.0065 EndZ=0
    g18: LineSegment [constr] StartX=21.6236 StartY=-35.0065 StartZ=0 EndX=19.0271 EndY=-32.7494 EndZ=0
    g19: LineSegment [constr] StartX=19.0271 StartY=-32.7494 StartZ=0 EndX=13.1803 EndY=-40.5083 EndZ=0
    g20: LineSegment [constr] StartX=13.1803 StartY=-40.5083 StartZ=0 EndX=13.5843 EndY=-40.7881 EndZ=0
    g21: LineSegment [constr] StartX=13.5843 StartY=-40.7881 StartZ=0 EndX=19.1591 EndY=-35.1151 EndZ=0
  constraints (45):
    c: Coincident(g2,g3)
    c: Coincident(g3,g4)
    c: Coincident(g4,g5)
    c: Coincident(g5,g6)
    c: Coincident(g6,g7)
    c: Coincident(g7,g8)
    c: Coincident(g8,g9)
    c: Coincident(g10,g11)
    c: Coincident(g10,g12)
    c: Coincident(g13,g9)
    c: Coincident(g13,g12)
    c: Coincident(g14,g2)
    c: Coincident(g14,g11)
    c: DistanceX(g8,g2) = 2.44158
    c: DistanceY(g2,g8) = 2.44158
    c: DistanceY(g12,g11) = 2.44158
    c: Equal(g4,g7)
    c: DistanceX(g9,g9) = 3.69936
    c: DistanceX(g9,g2) = 0.369936
    c: DistanceY(g3,g3) = 8.50853
    c: DistanceY(g8,g8) = 6.06695
    c: Angle(g3,g4) = 1.37532
    c: Symmetric(g8,g2,g15)
    c: Angle(g5,g4) = 0.776672
    c: DistanceY(g9,g12) = 8.87846
    c: DistanceX(g12,g13) = 0.739872
    c: DistanceX(g12,g12) = 1.99765
    c: Parallel(g6,g10)
    c: Coincident(g16,g17)
    c: Coincident(g17,g18)
    c: Coincident(g18,g19)
    c: Coincident(g19,g20)
    c: Coincident(g20,g21)
    c: Coincident(g21,g16)
    c: Parallel(g16,g18)
    c: DistanceY(g9,g16) = 4.14328
    c: Angle(g21,g16) = 1.63188
    c: Distance(g16,g16) = 1.88667
    c: Angle(g16,g9) = 0.715585
    c: Angle(g17,g16) = 1.5132
    c: Distance(g17,g17) = 1.70171
    c: Distance(g18,g18) = 3.44041
    c: Angle(g21,g20) = 1.74184
    c: Angle(g19,g18) = 1.50098
    c: Distance(g21,g21) = 7.95362
FEATURE [Image::ImagePlane] Screenshot_20260223_222318
  Placement = pos=(18.15,-9.5e-15,32.2) rot=(0,0.707107,0.707107;3.14159rad)
  XSize = 25.01
  YSize = 21.35
FEATURE [PartDesign::Pocket] Pocket024
  BaseFeature = -> Fillet052
  Direction = (0,-1,-2e-16)
  Length = 0.5
  Length2 = 5
  Placement = pos=(0,0,0) rot=(1,0,0;1.5708rad)
  Profile = -> Sketch044
  ReferenceAxis = -> Sketch044 [N_Axis]
  Refine = true
  Suppressed = false
  Type = 0
FEATURE [Sketcher::SketchObject] Sketch045
  ArcFitTolerance = 1e-06
  FullyConstrained = false
  MakeInternals = false
  MapMode = 5
  Placement = pos=(-0.5,13.5,-1) rot=(-1,0,0;1.5708rad)
  sketch-geometry (6):
    g0: LineSegment StartX=19.9974 StartY=-33.0287 StartZ=0 EndX=17.2831 EndY=-30.6947 EndZ=0
    g1: LineSegment StartX=17.2831 StartY=-30.6947 StartZ=0 EndX=11.0223 EndY=-38.9584 EndZ=0
    g2: LineSegment StartX=11.0223 StartY=-38.9584 StartZ=0 EndX=11.5209 EndY=-39.3211 EndZ=0
    g3: LineSegment StartX=11.5209 StartY=-39.3211 StartZ=0 EndX=17.3323 EndY=-33.2338 EndZ=0
    g4: LineSegment StartX=17.3323 StartY=-33.2338 StartZ=0 EndX=18.9724 EndY=-34.59 EndZ=0
    g5: LineSegment StartX=18.9724 StartY=-34.59 StartZ=0 EndX=19.9974 EndY=-33.0287 EndZ=0
  constraints (16):
    c: Coincident(g0,g1)
    c: Coincident(g1,g2)
    c: Coincident(g2,g3)
    c: Coincident(g3,g4)
    c: Coincident(g4,g5)
    c: Coincident(g5,g0)
    c: DistanceY(g3,g0) = 2.53902
    c: DistanceX(g0,g3) = 0.04918
    c: DistanceX(g3,g4) = 1.64011
    c: DistanceY(g0,g0) = 2.33401
    c: DistanceY(g5,g5) = 1.56126
    c: DistanceY(g3,g3) = 6.08735
    c: DistanceY(g1,g1) = 8.26366
    c: DistanceX(g5,g5) = 1.02507
    c: DistanceX(g1,g1) = 6.26082
    c: DistanceX(g3,g3) = 5.81137
FEATURE [PartDesign::Pocket] Pocket025
  BaseFeature = -> Pocket024
  Direction = (0,-1,-2e-16)
  Length = 0.5
  Length2 = 5
  Placement = pos=(0,0,0) rot=(1,0,0;1.5708rad)
  Profile = -> Sketch045
  ReferenceAxis = -> Sketch045 [N_Axis]
  Refine = true
  Suppressed = false
  Type = 0
FEATURE [Part::Part2DObjectPython] ShapeString  # Draft 2D object (typed FeaturePython)
  FontFile = /run/user/1000/doc/6a177af2/Hack-Bold.ttf
  Fuse = false
  Justification = 6
  JustificationReference = 0
  KeepLeftMargin = false
  MakeFace = true
  ObliqueAngle = 0
  Placement = pos=(0,0,0) rot=(1,0,0;1.5708rad)
  ScaleToSize = true
  Size = 7
  String = DiveChecker
  Tracking = 0
FEATURE [Sketcher::SketchObject] Sketch046
  ArcFitTolerance = 1e-06
  FullyConstrained = false
  MakeInternals = false
  Placement = pos=(6,-13.5,63) rot=(1,0,0;1.5708rad)
  sketch-geometry (176):
    g0: LineSegment StartX=4.68223 StartY=0 StartZ=0 EndX=4.68222 EndY=-0.991008 EndZ=0
    g1: LineSegment StartX=0 StartY=0 StartZ=0 EndX=4.68223 EndY=0 EndZ=0
    g2: LineSegment StartX=0 StartY=-0.991014 StartZ=0 EndX=0 EndY=0 EndZ=0
    g3: BSplineCurve PolesCount=3 KnotsCount=2 Degree=2 IsPeriodic=0
    g4: BSplineCurve PolesCount=3 KnotsCount=2 Degree=2 IsPeriodic=0
    g5: BSplineCurve PolesCount=3 KnotsCount=2 Degree=2 IsPeriodic=0
    g6: BSplineCurve PolesCount=3 KnotsCount=2 Degree=2 IsPeriodic=0
    g7: BSplineCurve PolesCount=3 KnotsCount=2 Degree=2 IsPeriodic=0
    g8: BSplineCurve PolesCount=3 KnotsCount=2 Degree=2 IsPeriodic=0
    g9: LineSegment StartX=0.834207 StartY=-0.925155 StartZ=0 EndX=0.834205 EndY=-1.17604 EndZ=0
    g10: LineSegment StartX=3.84802 StartY=-0.925155 StartZ=0 EndX=0.834207 EndY=-0.925155 EndZ=0
    g11: LineSegment StartX=3.84802 StartY=-1.17604 StartZ=0 EndX=3.84802 EndY=-0.925155 EndZ=0
    g12: BSplineCurve PolesCount=3 KnotsCount=2 Degree=2 IsPeriodic=0
    g13: BSplineCurve PolesCount=3 KnotsCount=2 Degree=2 IsPeriodic=0
    g14: BSplineCurve PolesCount=3 KnotsCount=2 Degree=2 IsPeriodic=0
    g15: BSplineCurve PolesCount=3 KnotsCount=2 Degree=2 IsPeriodic=0
    g16: LineSegment StartX=-0.037633 StartY=-6.97494 StartZ=0 EndX=-0.0376333 EndY=-5.98393 EndZ=0
    g17: LineSegment StartX=0.667994 StartY=-6.97494 StartZ=0 EndX=-0.037633 EndY=-6.97494 EndZ=0
    g18: LineSegment StartX=0.667994 StartY=-6.24109 StartZ=0 EndX=0.667994 EndY=-6.97494 EndZ=0
    g19: BSplineCurve PolesCount=3 KnotsCount=2 Degree=2 IsPeriodic=0
    g20: BSplineCurve PolesCount=3 KnotsCount=2 Degree=2 IsPeriodic=0
    g21: LineSegment StartX=3.51245 StartY=-5.67659 StartZ=0 EndX=1.42693 EndY=-5.67658 EndZ=0
    g22: LineSegment StartX=3.51245 StartY=-4.01444 StartZ=0 EndX=3.51245 EndY=-5.67659 EndZ=0
    g23: LineSegment StartX=2.80683 StartY=-4.01444 StartZ=0 EndX=3.51245 EndY=-4.01444 EndZ=0
    g24: LineSegment StartX=2.80683 StartY=-4.7577 StartZ=0 EndX=2.80683 EndY=-4.01444 EndZ=0
    g25: LineSegment StartX=1.42693 StartY=-4.7577 StartZ=0 EndX=2.80683 EndY=-4.7577 EndZ=0
    g26: BSplineCurve PolesCount=3 KnotsCount=2 Degree=2 IsPeriodic=0
    g27: BSplineCurve PolesCount=3 KnotsCount=2 Degree=2 IsPeriodic=0
    g28: LineSegment StartX=3.92956 StartY=-5.5825 StartZ=0 EndX=3.92956 EndY=-4.85178 EndZ=0
    g29: BSplineCurve PolesCount=3 KnotsCount=2 Degree=2 IsPeriodic=0
    g30: LineSegment StartX=4.90803 StartY=-5.67659 StartZ=0 EndX=4.02364 EndY=-5.67658 EndZ=0
    g31: BSplineCurve PolesCount=3 KnotsCount=2 Degree=2 IsPeriodic=0
    g32: LineSegment StartX=5.00211 StartY=-4.85178 StartZ=0 EndX=5.00211 EndY=-5.5825 EndZ=0
    g33: BSplineCurve PolesCount=3 KnotsCount=2 Degree=2 IsPeriodic=0
    g34: LineSegment StartX=4.02364 StartY=-4.7577 StartZ=0 EndX=4.90802 EndY=-4.75771 EndZ=0
    g35: LineSegment StartX=3.51245 StartY=-7.55533 StartZ=0 EndX=3.51245 EndY=-8.48676 EndZ=0
    g36: LineSegment StartX=0 StartY=-8.67179 StartZ=0 EndX=3.51245 EndY=-7.55533 EndZ=0
    g37: LineSegment StartX=0 StartY=-9.80393 StartZ=0 EndX=0 EndY=-8.67179 EndZ=0
    g38: LineSegment StartX=3.51245 StartY=-10.9204 StartZ=0 EndX=0 EndY=-9.80393 EndZ=0
    g39: LineSegment StartX=3.51245 StartY=-9.98896 StartZ=0 EndX=3.51245 EndY=-10.9204 EndZ=0
    g40: LineSegment StartX=0.771485 StartY=-9.23629 StartZ=0 EndX=3.51245 EndY=-9.98896 EndZ=0
    g41: LineSegment StartX=3.51245 StartY=-8.48676 StartZ=0 EndX=0.771485 EndY=-9.23629 EndZ=0
    g42: BSplineCurve PolesCount=3 KnotsCount=2 Degree=2 IsPeriodic=0
    g43: BSplineCurve PolesCount=3 KnotsCount=2 Degree=2 IsPeriodic=0
    g44: LineSegment StartX=1.0161 StartY=-14.5961 StartZ=0 EndX=0.172486 EndY=-14.5961 EndZ=0
    g45: BSplineCurve PolesCount=3 KnotsCount=2 Degree=2 IsPeriodic=0
    g46: BSplineCurve PolesCount=3 KnotsCount=2 Degree=2 IsPeriodic=0
    g47: LineSegment StartX=1.45829 StartY=-14.7435 StartZ=0 EndX=1.4583 EndY=-12.3633 EndZ=0
    g48: LineSegment StartX=1.83149 StartY=-14.7435 StartZ=0 EndX=1.45829 EndY=-14.7435 EndZ=0
    g49: BSplineCurve PolesCount=3 KnotsCount=2 Degree=2 IsPeriodic=0
    g50: BSplineCurve PolesCount=3 KnotsCount=2 Degree=2 IsPeriodic=0
    g51: BSplineCurve PolesCount=3 KnotsCount=2 Degree=2 IsPeriodic=0
    g52: BSplineCurve PolesCount=3 KnotsCount=2 Degree=2 IsPeriodic=0
    g53: BSplineCurve PolesCount=3 KnotsCount=2 Degree=2 IsPeriodic=0
    g54: BSplineCurve PolesCount=3 KnotsCount=2 Degree=2 IsPeriodic=0
    g55: BSplineCurve PolesCount=3 KnotsCount=2 Degree=2 IsPeriodic=0
    g56: BSplineCurve PolesCount=3 KnotsCount=2 Degree=2 IsPeriodic=0
    g57: LineSegment StartX=2.14824 StartY=-12.3726 StartZ=0 EndX=2.14824 EndY=-13.8184 EndZ=0
    g58: BSplineCurve PolesCount=3 KnotsCount=2 Degree=2 IsPeriodic=0
    g59: BSplineCurve PolesCount=3 KnotsCount=2 Degree=2 IsPeriodic=0
    g60: BSplineCurve PolesCount=3 KnotsCount=2 Degree=2 IsPeriodic=0
    g61: BSplineCurve PolesCount=3 KnotsCount=2 Degree=2 IsPeriodic=0
    g62: BSplineCurve PolesCount=3 KnotsCount=2 Degree=2 IsPeriodic=0
    g63: BSplineCurve PolesCount=3 KnotsCount=2 Degree=2 IsPeriodic=0
    g64: LineSegment StartX=1.1635 StartY=-18.3942 StartZ=0 EndX=0.134853 EndY=-18.3942 EndZ=0
    g65: BSplineCurve PolesCount=3 KnotsCount=2 Degree=2 IsPeriodic=0
    g66: BSplineCurve PolesCount=3 KnotsCount=2 Degree=2 IsPeriodic=0
    g67: BSplineCurve PolesCount=3 KnotsCount=2 Degree=2 IsPeriodic=0
    g68: BSplineCurve PolesCount=3 KnotsCount=2 Degree=2 IsPeriodic=0
    g69: BSplineCurve PolesCount=3 KnotsCount=2 Degree=2 IsPeriodic=0
    g70: BSplineCurve PolesCount=3 KnotsCount=2 Degree=2 IsPeriodic=0
    g71: BSplineCurve PolesCount=3 KnotsCount=2 Degree=2 IsPeriodic=0
    g72: BSplineCurve PolesCount=3 KnotsCount=2 Degree=2 IsPeriodic=0
    g73: BSplineCurve PolesCount=3 KnotsCount=2 Degree=2 IsPeriodic=0
    g74: BSplineCurve PolesCount=3 KnotsCount=2 Degree=2 IsPeriodic=0
    g75: BSplineCurve PolesCount=3 KnotsCount=2 Degree=2 IsPeriodic=0
    g76: LineSegment StartX=4.5411 StartY=-18.3942 StartZ=0 EndX=3.51245 EndY=-18.3942 EndZ=0
    g77: BSplineCurve PolesCount=3 KnotsCount=2 Degree=2 IsPeriodic=0
    g78: BSplineCurve PolesCount=3 KnotsCount=2 Degree=2 IsPeriodic=0
    g79: BSplineCurve PolesCount=3 KnotsCount=2 Degree=2 IsPeriodic=0
    g80: BSplineCurve PolesCount=3 KnotsCount=2 Degree=2 IsPeriodic=0
    g81: BSplineCurve PolesCount=3 KnotsCount=2 Degree=2 IsPeriodic=0
    g82: LineSegment StartX=4.8798 StartY=-19.445 StartZ=0 EndX=4.8798 EndY=-20.3576 EndZ=0
    g83: LineSegment StartX=0 StartY=-19.445 StartZ=0 EndX=4.8798 EndY=-19.445 EndZ=0
    g84: LineSegment StartX=0 StartY=-20.3576 StartZ=0 EndX=0 EndY=-19.445 EndZ=0
    g85: LineSegment StartX=2.01025 StartY=-20.3576 StartZ=0 EndX=0 EndY=-20.3576 EndZ=0
    g86: BSplineCurve PolesCount=3 KnotsCount=2 Degree=2 IsPeriodic=0
    g87: BSplineCurve PolesCount=3 KnotsCount=2 Degree=2 IsPeriodic=0
    g88: BSplineCurve PolesCount=3 KnotsCount=2 Degree=2 IsPeriodic=0
    g89: BSplineCurve PolesCount=3 KnotsCount=2 Degree=2 IsPeriodic=0
    g90: LineSegment StartX=0 StartY=-21.3517 StartZ=0 EndX=2.13883 EndY=-21.3518 EndZ=0
    g91: LineSegment StartX=0 StartY=-22.2644 StartZ=0 EndX=0 EndY=-21.3517 EndZ=0
    g92: LineSegment StartX=2.27996 StartY=-22.2644 StartZ=0 EndX=0 EndY=-22.2644 EndZ=0
    g93: BSplineCurve PolesCount=3 KnotsCount=2 Degree=2 IsPeriodic=0
    g94: BSplineCurve PolesCount=3 KnotsCount=2 Degree=2 IsPeriodic=0
    g95: BSplineCurve PolesCount=3 KnotsCount=2 Degree=2 IsPeriodic=0
    g96: BSplineCurve PolesCount=3 KnotsCount=2 Degree=2 IsPeriodic=0
    g97: LineSegment StartX=4.8798 StartY=-20.3576 StartZ=0 EndX=2.98559 EndY=-20.3576 EndZ=0
    g98: BSplineCurve PolesCount=3 KnotsCount=2 Degree=2 IsPeriodic=0
    g99: BSplineCurve PolesCount=3 KnotsCount=2 Degree=2 IsPeriodic=0
    g100: LineSegment StartX=1.0161 StartY=-26.1973 StartZ=0 EndX=0.172486 EndY=-26.1972 EndZ=0
    g101: BSplineCurve PolesCount=3 KnotsCount=2 Degree=2 IsPeriodic=0
    g102: BSplineCurve PolesCount=3 KnotsCount=2 Degree=2 IsPeriodic=0
    g103: LineSegment StartX=1.4583 StartY=-26.3447 StartZ=0 EndX=1.4583 EndY=-23.9644 EndZ=0
    g104: LineSegment StartX=1.8315 StartY=-26.3447 StartZ=0 EndX=1.4583 EndY=-26.3447 EndZ=0
    g105: BSplineCurve PolesCount=3 KnotsCount=2 Degree=2 IsPeriodic=0
    g106: BSplineCurve PolesCount=3 KnotsCount=2 Degree=2 IsPeriodic=0
    g107: BSplineCurve PolesCount=3 KnotsCount=2 Degree=2 IsPeriodic=0
    g108: BSplineCurve PolesCount=3 KnotsCount=2 Degree=2 IsPeriodic=0
    g109: BSplineCurve PolesCount=3 KnotsCount=2 Degree=2 IsPeriodic=0
    g110: BSplineCurve PolesCount=3 KnotsCount=2 Degree=2 IsPeriodic=0
    g111: BSplineCurve PolesCount=3 KnotsCount=2 Degree=2 IsPeriodic=0
    g112: BSplineCurve PolesCount=3 KnotsCount=2 Degree=2 IsPeriodic=0
    g113: LineSegment StartX=2.14824 StartY=-23.9737 StartZ=0 EndX=2.14824 EndY=-25.4195 EndZ=0
    g114: BSplineCurve PolesCount=3 KnotsCount=2 Degree=2 IsPeriodic=0
    g115: BSplineCurve PolesCount=3 KnotsCount=2 Degree=2 IsPeriodic=0
    g116: BSplineCurve PolesCount=3 KnotsCount=2 Degree=2 IsPeriodic=0
    g117: BSplineCurve PolesCount=3 KnotsCount=2 Degree=2 IsPeriodic=0
    g118: BSplineCurve PolesCount=3 KnotsCount=2 Degree=2 IsPeriodic=0
    g119: LineSegment StartX=1.02238 StartY=-29.9044 StartZ=0 EndX=0.178759 EndY=-29.9043 EndZ=0
    g120: BSplineCurve PolesCount=3 KnotsCount=2 Degree=2 IsPeriodic=0
    g121: BSplineCurve PolesCount=3 KnotsCount=2 Degree=2 IsPeriodic=0
    g122: BSplineCurve PolesCount=3 KnotsCount=2 Degree=2 IsPeriodic=0
    g123: BSplineCurve PolesCount=3 KnotsCount=2 Degree=2 IsPeriodic=0
    g124: BSplineCurve PolesCount=3 KnotsCount=2 Degree=2 IsPeriodic=0
    g125: BSplineCurve PolesCount=3 KnotsCount=2 Degree=2 IsPeriodic=0
    g126: LineSegment StartX=3.33369 StartY=-29.9044 StartZ=0 EndX=2.4932 EndY=-29.9043 EndZ=0
    g127: BSplineCurve PolesCount=3 KnotsCount=2 Degree=2 IsPeriodic=0
    g128: BSplineCurve PolesCount=3 KnotsCount=2 Degree=2 IsPeriodic=0
    g129: BSplineCurve PolesCount=3 KnotsCount=2 Degree=2 IsPeriodic=0
    g130: BSplineCurve PolesCount=3 KnotsCount=2 Degree=2 IsPeriodic=0
    g131: LineSegment StartX=4.8798 StartY=-31.0524 StartZ=0 EndX=4.8798 EndY=-31.9713 EndZ=0
    g132: LineSegment StartX=0 StartY=-31.0524 StartZ=0 EndX=4.8798 EndY=-31.0524 EndZ=0
    g133: LineSegment StartX=0 StartY=-31.9713 StartZ=0 EndX=0 EndY=-31.0524 EndZ=0
    g134: LineSegment StartX=1.34226 StartY=-31.9713 StartZ=0 EndX=0 EndY=-31.9713 EndZ=0
    g135: LineSegment StartX=1.64333 StartY=-32.2849 StartZ=0 EndX=1.34226 EndY=-31.9713 EndZ=0
    g136: LineSegment StartX=0 StartY=-33.2477 StartZ=0 EndX=1.64333 EndY=-32.2849 EndZ=0
    g137: LineSegment StartX=0 StartY=-34.2638 StartZ=0 EndX=0 EndY=-33.2477 EndZ=0
    g138: LineSegment StartX=2.20156 StartY=-32.8588 StartZ=0 EndX=0 EndY=-34.2638 EndZ=0
    g139: LineSegment StartX=3.51245 StartY=-34.1885 StartZ=0 EndX=2.20156 EndY=-32.8588 EndZ=0
    g140: LineSegment StartX=3.51245 StartY=-33.0752 StartZ=0 EndX=3.51245 EndY=-34.1885 EndZ=0
    g141: LineSegment StartX=2.31759 StartY=-31.9713 StartZ=0 EndX=3.51245 EndY=-33.0752 EndZ=0
    g142: LineSegment StartX=4.8798 StartY=-31.9713 StartZ=0 EndX=2.31759 EndY=-31.9713 EndZ=0
    g143: BSplineCurve PolesCount=3 KnotsCount=2 Degree=2 IsPeriodic=0
    g144: BSplineCurve PolesCount=3 KnotsCount=2 Degree=2 IsPeriodic=0
    g145: LineSegment StartX=1.0161 StartY=-37.7984 StartZ=0 EndX=0.172487 EndY=-37.7985 EndZ=0
    g146: BSplineCurve PolesCount=3 KnotsCount=2 Degree=2 IsPeriodic=0
    g147: BSplineCurve PolesCount=3 KnotsCount=2 Degree=2 IsPeriodic=0
    g148: LineSegment StartX=1.4583 StartY=-37.9458 StartZ=0 EndX=1.4583 EndY=-35.5655 EndZ=0
    g149: LineSegment StartX=1.8315 StartY=-37.9458 StartZ=0 EndX=1.4583 EndY=-37.9458 EndZ=0
    g150: BSplineCurve PolesCount=3 KnotsCount=2 Degree=2 IsPeriodic=0
    g151: BSplineCurve PolesCount=3 KnotsCount=2 Degree=2 IsPeriodic=0
    g152: BSplineCurve PolesCount=3 KnotsCount=2 Degree=2 IsPeriodic=0
    g153: BSplineCurve PolesCount=3 KnotsCount=2 Degree=2 IsPeriodic=0
    g154: BSplineCurve PolesCount=3 KnotsCount=2 Degree=2 IsPeriodic=0
    g155: BSplineCurve PolesCount=3 KnotsCount=2 Degree=2 IsPeriodic=0
    g156: BSplineCurve PolesCount=3 KnotsCount=2 Degree=2 IsPeriodic=0
    g157: BSplineCurve PolesCount=3 KnotsCount=2 Degree=2 IsPeriodic=0
    g158: LineSegment StartX=2.14824 StartY=-35.5749 StartZ=0 EndX=2.14824 EndY=-37.0206 EndZ=0
    g159: BSplineCurve PolesCount=3 KnotsCount=2 Degree=2 IsPeriodic=0
    g160: BSplineCurve PolesCount=3 KnotsCount=2 Degree=2 IsPeriodic=0
    g161: BSplineCurve PolesCount=3 KnotsCount=2 Degree=2 IsPeriodic=0
    g162: LineSegment StartX=3.51245 StartY=-38.9966 StartZ=0 EndX=3.51245 EndY=-39.8245 EndZ=0
    g163: LineSegment StartX=0 StartY=-38.9966 StartZ=0 EndX=3.51245 EndY=-38.9966 EndZ=0
    g164: LineSegment StartX=1e-06 StartY=-39.9155 StartZ=0 EndX=0 EndY=-38.9966 EndZ=0
    g165: LineSegment StartX=1.61824 StartY=-39.9155 StartZ=0 EndX=1e-06 EndY=-39.9155 EndZ=0
    g166: BSplineCurve PolesCount=3 KnotsCount=2 Degree=2 IsPeriodic=0
    g167: BSplineCurve PolesCount=3 KnotsCount=2 Degree=2 IsPeriodic=0
    g168: BSplineCurve PolesCount=3 KnotsCount=2 Degree=2 IsPeriodic=0
    g169: BSplineCurve PolesCount=3 KnotsCount=2 Degree=2 IsPeriodic=0
    g170: BSplineCurve PolesCount=3 KnotsCount=2 Degree=2 IsPeriodic=0
    g171: LineSegment StartX=3.41837 StartY=-41.6937 StartZ=0 EndX=2.54339 EndY=-41.6937 EndZ=0
    g172: BSplineCurve PolesCount=3 KnotsCount=2 Degree=2 IsPeriodic=0
    g173: BSplineCurve PolesCount=3 KnotsCount=2 Degree=2 IsPeriodic=0
    g174: BSplineCurve PolesCount=3 KnotsCount=2 Degree=2 IsPeriodic=0
    g175: LineSegment StartX=3.51245 StartY=-39.8245 StartZ=0 EndX=2.96677 EndY=-39.9154 EndZ=0
  constraints (176):
    c: Coincident(g0,g1)
    c: Coincident(g1,g2)
    c: Coincident(g2,g3)
    c: Coincident(g3,g4)
    c: Coincident(g4,g5)
    c: Coincident(g5,g6)
    c: Coincident(g6,g7)
    c: Coincident(g7,g0)
    c: Coincident(g8,g9)
    c: Coincident(g9,g10)
    c: Coincident(g10,g11)
    c: Coincident(g11,g12)
    c: Coincident(g12,g13)
    c: Coincident(g13,g14)
    c: Coincident(g14,g8)
    c: Coincident(g15,g16)
    c: Coincident(g16,g17)
    c: Coincident(g17,g18)
    c: Coincident(g18,g19)
    c: Coincident(g19,g20)
    c: Coincident(g20,g21)
    c: Coincident(g21,g22)
    c: Coincident(g22,g23)
    c: Coincident(g23,g24)
    c: Coincident(g24,g25)
    c: Coincident(g25,g26)
    c: Coincident(g26,g15)
    c: Coincident(g27,g28)
    c: Coincident(g28,g29)
    c: Coincident(g29,g30)
    c: Coincident(g30,g31)
    c: Coincident(g31,g32)
    c: Coincident(g32,g33)
    c: Coincident(g33,g34)
    c: Coincident(g34,g27)
    c: Coincident(g35,g36)
    c: Coincident(g36,g37)
    c: Coincident(g37,g38)
    c: Coincident(g38,g39)
    c: Coincident(g39,g40)
    c: Coincident(g40,g41)
    c: Coincident(g41,g35)
    c: Coincident(g42,g43)
    c: Coincident(g43,g44)
    c: Coincident(g44,g45)
    c: Coincident(g45,g46)
    c: Coincident(g46,g47)
    c: Coincident(g47,g48)
    c: Coincident(g48,g49)
    c: Coincident(g49,g50)
    c: Coincident(g50,g51)
    c: Coincident(g51,g52)
    c: Coincident(g52,g53)
    c: Coincident(g53,g54)
    c: Coincident(g54,g55)
    c: Coincident(g55,g42)
    c: Coincident(g56,g57)
    c: Coincident(g57,g58)
    c: Coincident(g58,g59)
    c: Coincident(g59,g60)
    c: Coincident(g60,g56)
    c: Coincident(g61,g62)
    c: Coincident(g62,g63)
    c: Coincident(g63,g64)
    c: Coincident(g64,g65)
    c: Coincident(g65,g66)
    c: Coincident(g66,g67)
    c: Coincident(g67,g68)
    c: Coincident(g68,g69)
    c: Coincident(g69,g70)
    c: Coincident(g70,g71)
    c: Coincident(g71,g72)
    c: Coincident(g72,g73)
    c: Coincident(g73,g74)
    c: Coincident(g74,g75)
    c: Coincident(g75,g76)
    c: Coincident(g76,g77)
    c: Coincident(g77,g78)
    c: Coincident(g78,g79)
    c: Coincident(g79,g80)
    c: Coincident(g80,g81)
    c: Coincident(g81,g61)
    c: Coincident(g82,g83)
    c: Coincident(g83,g84)
    c: Coincident(g84,g85)
    c: Coincident(g85,g86)
    c: Coincident(g86,g87)
    c: Coincident(g87,g88)
    c: Coincident(g88,g89)
    c: Coincident(g89,g90)
    c: Coincident(g90,g91)
    c: Coincident(g91,g92)
    c: Coincident(g92,g93)
    c: Coincident(g93,g94)
    c: Coincident(g94,g95)
    c: Coincident(g95,g96)
    c: Coincident(g96,g97)
    c: Coincident(g97,g82)
    c: Coincident(g98,g99)
    c: Coincident(g99,g100)
    c: Coincident(g100,g101)
    c: Coincident(g101,g102)
    c: Coincident(g102,g103)
    c: Coincident(g103,g104)
    c: Coincident(g104,g105)
    c: Coincident(g105,g106)
    c: Coincident(g106,g107)
    c: Coincident(g107,g108)
    c: Coincident(g108,g109)
    c: Coincident(g109,g110)
    c: Coincident(g110,g111)
    c: Coincident(g111,g98)
    c: Coincident(g112,g113)
    c: Coincident(g113,g114)
    c: Coincident(g114,g115)
    c: Coincident(g115,g116)
    c: Coincident(g116,g112)
    c: Coincident(g117,g118)
    c: Coincident(g118,g119)
    c: Coincident(g119,g120)
    c: Coincident(g120,g121)
    c: Coincident(g121,g122)
    c: Coincident(g122,g123)
    c: Coincident(g123,g124)
    c: Coincident(g124,g125)
    c: Coincident(g125,g126)
    c: Coincident(g126,g127)
    c: Coincident(g127,g128)
    c: Coincident(g128,g129)
    c: Coincident(g129,g130)
    c: Coincident(g130,g117)
    c: Coincident(g131,g132)
    c: Coincident(g132,g133)
    c: Coincident(g133,g134)
    c: Coincident(g134,g135)
    c: Coincident(g135,g136)
    c: Coincident(g136,g137)
    c: Coincident(g137,g138)
    c: Coincident(g138,g139)
    c: Coincident(g139,g140)
    c: Coincident(g140,g141)
    c: Coincident(g141,g142)
    c: Coincident(g142,g131)
    c: Coincident(g143,g144)
    c: Coincident(g144,g145)
    c: Coincident(g145,g146)
    c: Coincident(g146,g147)
    c: Coincident(g147,g148)
    c: Coincident(g148,g149)
    c: Coincident(g149,g150)
    c: Coincident(g150,g151)
    c: Coincident(g151,g152)
    c: Coincident(g152,g153)
    c: Coincident(g153,g154)
    c: Coincident(g154,g155)
    c: Coincident(g155,g156)
    c: Coincident(g156,g143)
    c: Coincident(g157,g158)
    c: Coincident(g158,g159)
    c: Coincident(g159,g160)
    c: Coincident(g160,g161)
    c: Coincident(g161,g157)
    c: Coincident(g162,g163)
    c: Coincident(g163,g164)
    c: Coincident(g164,g165)
    c: Coincident(g165,g166)
    c: Coincident(g166,g167)
    c: Coincident(g167,g168)
    c: Coincident(g168,g169)
    c: Coincident(g169,g170)
    c: Coincident(g170,g171)
    c: Coincident(g171,g172)
    c: Coincident(g172,g173)
    c: Coincident(g173,g174)
    c: Coincident(g174,g175)
    c: Coincident(g175,g162)
FEATURE [PartDesign::Pocket] Pocket026
  BaseFeature = -> Pocket025
  Direction = (0,1,-2e-16)
  Length = 1
  Length2 = 5
  Midplane = true
  Placement = pos=(0,0,0) rot=(1,0,0;1.5708rad)
  Profile = -> Sketch046
  ReferenceAxis = -> Sketch046 [N_Axis]
  Refine = true
  Suppressed = false
  Type = 0
FEATURE [PartDesign::Fillet] Fillet053
  Base = -> Pocket026 [Edge688,Edge692]
  BaseFeature = -> Pocket026
  Placement = pos=(0,0,0) rot=(1,0,0;1.5708rad)
  Radius = 0.125
  Refine = true
  SupportTransform = false
  Suppressed = false
  UseAllEdges = false
FEATURE [PartDesign::Fillet] Fillet054
  Base = -> Fillet053 [Edge42]
  BaseFeature = -> Fillet053
  Placement = pos=(0,0,0) rot=(1,0,0;1.5708rad)
  Radius = 0.25
  Refine = true
  SupportTransform = false
  Suppressed = false
  UseAllEdges = false
FEATURE [PartDesign::Fillet] Fillet055
  Base = -> Fillet054 [Edge51,Edge45,Edge49,Edge55,Edge77,Edge81,Edge79,Edge75,Edge71,Edge67,Edge62,Edge65,Edge58,Edge70,Edge64,Edge83]
  BaseFeature = -> Fillet054
  Placement = pos=(0,0,0) rot=(1,0,0;1.5708rad)
  Radius = 0.125
  Refine = true
  SupportTransform = false
  Suppressed = false
  UseAllEdges = false
FEATURE [PartDesign::Fillet] Fillet056
  Base = -> Fillet055 [Edge67,Edge103,Edge123,Edge93]
  BaseFeature = -> Fillet055
  Placement = pos=(0,0,0) rot=(1,0,0;1.5708rad)
  Radius = 3
  Refine = true
  SupportTransform = false
  Suppressed = false
  UseAllEdges = false
FEATURE [PartDesign::Fillet] Fillet057
  Base = -> Fillet056 [Edge112,Edge29]
  BaseFeature = -> Fillet056
  Placement = pos=(0,0,0) rot=(1,0,0;1.5708rad)
  Radius = 0.125
  Refine = true
  SupportTransform = false
  Suppressed = false
  UseAllEdges = false
FEATURE [PartDesign::Pad] Pad014
  BaseFeature = -> Fillet057
  Direction = (0,-1,-2e-16)
  Length = 0.5
  Length2 = 10
  Placement = pos=(0,0,0) rot=(1,0,0;1.5708rad)
  Profile = -> Fillet057 [Face373]
  Refine = true
  Suppressed = false
  Type = 0
FEATURE [PartDesign::Body] Body  label="Main-body"
  AllowCompound = true
  Group = -> [Sketch,Pad,Fillet,Fillet001,Sketch006,Pocket,Sketch008,Pocket001,Sketch009,Pocket002,Sketch010,Pocket003,Fillet002,Fillet003,Fillet004,Fillet005,Fillet006,Fillet007,Fillet008,Fillet009,Fillet010,Fillet011,Fillet012,Fillet013,Fillet014,Fillet015,Sketch021,Pocket007,Sketch038,Pocket018,Sketch041,Pocket021,Fillet045,Pad012,Pocket022,Fillet046,Fillet047,Fillet048,Sketch042,Pad013,Fillet051,Fillet052,+12 more]
  Origin = -> Origin
  Tip = -> Pad014
